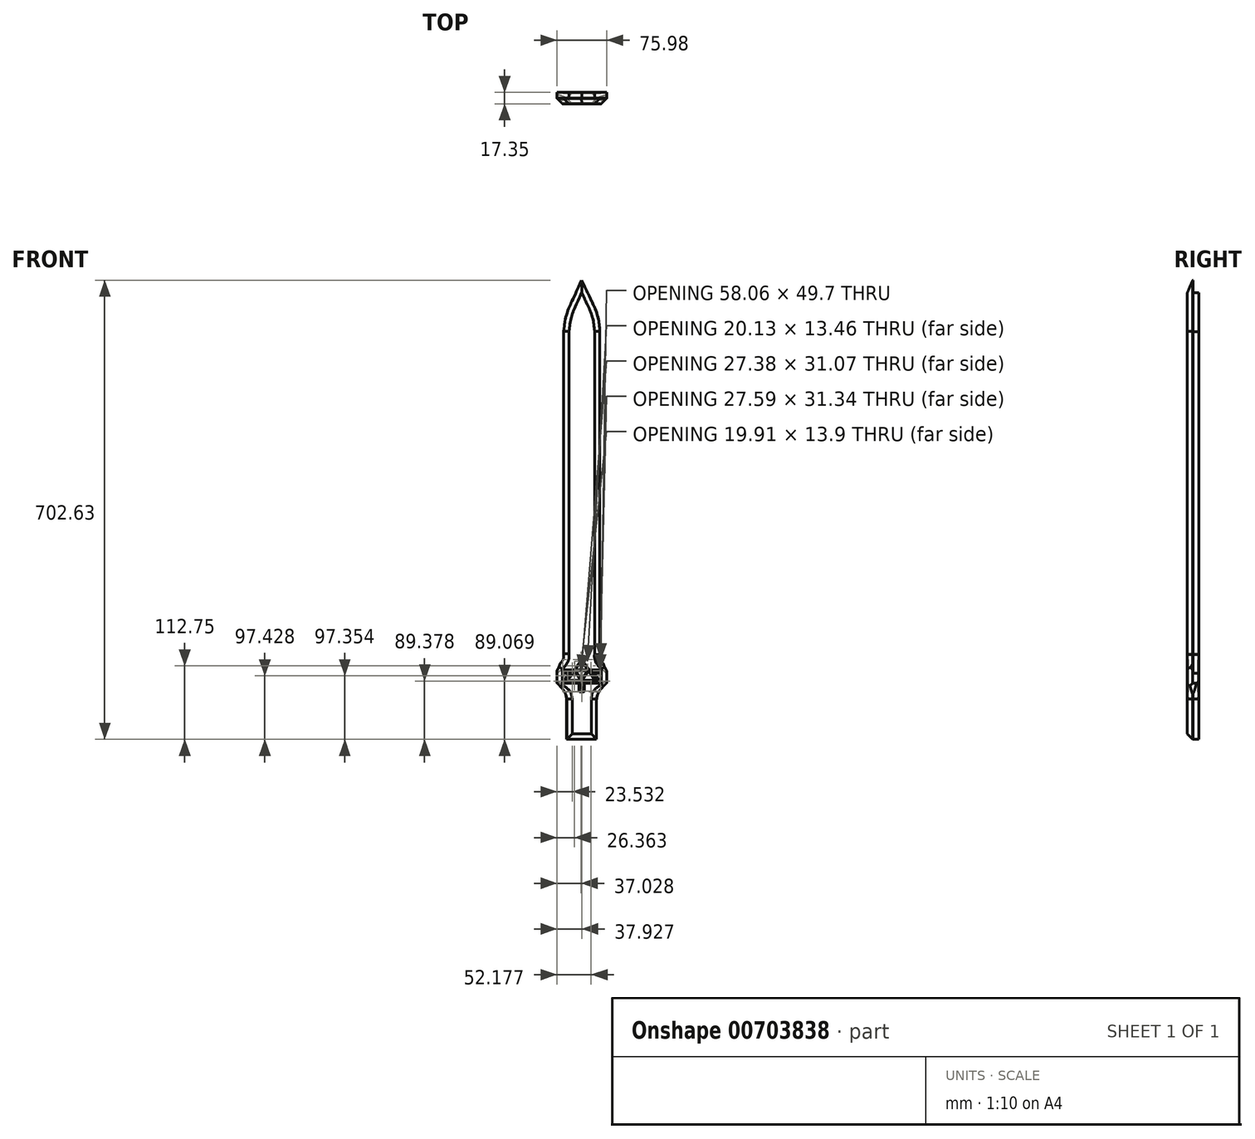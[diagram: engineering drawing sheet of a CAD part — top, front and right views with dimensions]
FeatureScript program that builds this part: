
annotation { "Feature Type Name" : "Feature", "Feature Type Description" : "" }
export const myFeature = defineFeature(function(context is Context, id is Id, definition is map)
    precondition{}
    {
        {
            var Q0;
            Q0=qCreatedBy(makeId("Front.planeOp"),FACE);
            var sketch = newSketch(context, id + "F0", { "sketchPlane" : qUnion([Q0])});
            skLineSegment(sketch, "E0", {"start": v(-23.18, 89.36) * mm, "end": v(-23.18, 27.94) * mm});
            skLineSegment(sketch, "E1", {"start": v(-23.18, 27.94) * mm, "end": v(22.75, 27.94) * mm});
            skLineSegment(sketch, "E2", {"start": v(22.75, 27.94) * mm, "end": v(22.75, 89.36) * mm});
            skFitSpline(sketch, "E3", {"points": [v(-23.18, 89.36) * mm, v(-25.2, 98.78) * mm, v(-29.58, 105.34) * mm, v(-34.12, 110.56) * mm, v(-37.82, 114.26) * mm], "startDerivative": vector(-4.45, 34.79) * mm, "endDerivative": vector(-17.26, 16.67) * mm});
            skFitSpline(sketch, "E4", {"points": [v(22.75, 89.36) * mm, v(24.94, 98.27) * mm, v(29.82, 105.5) * mm, v(34.53, 110.56) * mm, v(38.16, 114.22) * mm], "startDerivative": vector(5.26, 33.12) * mm, "endDerivative": vector(16.94, 16.97) * mm});
            skLineSegment(sketch, "E5", {"start": v(-37.82, 114.26) * mm, "end": v(-37.82, 132.92) * mm});
            skLineSegment(sketch, "E6", {"start": v(38.16, 114.22) * mm, "end": v(38.16, 132.92) * mm});
            skFitSpline(sketch, "E7", {"points": [v(-37.82, 132.92) * mm, v(-34.87, 138.92) * mm, v(-32.96, 144.16) * mm, v(-31.8, 152.09) * mm, v(-31.68, 159) * mm], "startDerivative": vector(12.58, 24.9) * mm, "endDerivative": vector(-0.2, 26.4) * mm});
            skFitSpline(sketch, "E8", {"points": [v(38.16, 132.92) * mm, v(35.43, 137.9) * mm, v(32.87, 144.8) * mm, v(31.98, 152.47) * mm, v(31.85, 157.97) * mm], "startDerivative": vector(-11.86, 20.42) * mm, "endDerivative": vector(-0.27, 22.84) * mm});
            skLineSegment(sketch, "E9", {"start": v(-31.68, 159) * mm, "end": v(-31.68, 655.53) * mm});
            skLineSegment(sketch, "E10", {"start": v(31.85, 157.97) * mm, "end": v(31.87, 655.53) * mm});
            skFitSpline(sketch, "E11", {"points": [v(0, 770.67) * mm, v(5.75, 755.45) * mm, v(13.9, 732.8) * mm, v(20.44, 712.09) * mm, v(27.87, 687.66) * mm, v(30.7, 671.38) * mm, v(31.87, 655.53) * mm], "startDerivative": vector(35.97, -94.67) * mm, "endDerivative": vector(6.36, -107.63) * mm});
            skFitSpline(sketch, "E12", {"points": [v(0, 770.67) * mm, v(-7.17, 751.02) * mm, v(-17.08, 723.77) * mm, v(-25.22, 697.22) * mm, v(-28.94, 682) * mm, v(-31.68, 655.53) * mm], "startDerivative": vector(-36.3, -100.65) * mm, "endDerivative": vector(-10.82, -136.16) * mm});
            skSolve(sketch);
        }
        {
            var Q0;
            Q0=makeQuery(id+"F0.imprint","IMPRINT",FACE,{"disambiguationData":[TD([[makeQuery(id+"F0.imprint","IMPRINT",EDGE,{"derivedFrom":sQuery(id+"F0.wireOp",EDGE,"E0")}),1.0]])]});
            extrude(context, id + "F1", {"entities" : qUnion([Q0]), "depth" : 0.25 * mm, "offsetDistance" : 25.4 * mm});
        }
        {
            var Q0;
            Q0=makeQuery(id+"F1.opExtrude","CAP_FACE",FACE,{"disambiguationData":[OSD([sQuery(id+"F0.wireOp",EDGE,"E0"),sQuery(id+"F0.wireOp",EDGE,"E1"),sQuery(id+"F0.wireOp",EDGE,"E2"),sQuery(id+"F0.wireOp",EDGE,"E3"),sQuery(id+"F0.wireOp",EDGE,"E4"),sQuery(id+"F0.wireOp",EDGE,"E5"),sQuery(id+"F0.wireOp",EDGE,"E6"),sQuery(id+"F0.wireOp",EDGE,"E7"),sQuery(id+"F0.wireOp",EDGE,"E8"),sQuery(id+"F0.wireOp",EDGE,"E9"),sQuery(id+"F0.wireOp",EDGE,"E10"),sQuery(id+"F0.wireOp",EDGE,"E11"),sQuery(id+"F0.wireOp",EDGE,"E12")])],"isStart":true});
            extrude(context, id + "F2", {"entities" : qUnion([Q0]), "operationType" : NewBodyOperationType.ADD, "depth" : 0.25 * mm, "offsetDistance" : 25.4 * mm});
        }
        {
            var Q0;
            Q0=makeQuery(id+"F2.opExtrude","CAP_FACE",FACE,{"disambiguationData":[OSD([sQuery(id+"F0.wireOp",EDGE,"E0"),sQuery(id+"F0.wireOp",EDGE,"E1"),sQuery(id+"F0.wireOp",EDGE,"E2"),sQuery(id+"F0.wireOp",EDGE,"E3"),sQuery(id+"F0.wireOp",EDGE,"E4"),sQuery(id+"F0.wireOp",EDGE,"E5"),sQuery(id+"F0.wireOp",EDGE,"E6"),sQuery(id+"F0.wireOp",EDGE,"E7"),sQuery(id+"F0.wireOp",EDGE,"E8"),sQuery(id+"F0.wireOp",EDGE,"E9"),sQuery(id+"F0.wireOp",EDGE,"E10"),sQuery(id+"F0.wireOp",EDGE,"E11"),sQuery(id+"F0.wireOp",EDGE,"E12")])],"isStart":false});
            var sketch = newSketch(context, id + "F3", { "sketchPlane" : qUnion([Q0])});
            skLineSegment(sketch, "E13", {"start": v(-14.88, 27.94) * mm, "end": v(-14.88, 90.23) * mm});
            skFitSpline(sketch, "E14", {"points": [v(-14.88, 90.23) * mm, v(-16.73, 99.87) * mm, v(-22.43, 106.47) * mm, v(-31.13, 113.07) * mm, v(-38.16, 117.57) * mm], "startDerivative": vector(-3.35, 40.52) * mm, "endDerivative": vector(-28.93, 17.8) * mm});
            skLineSegment(sketch, "E15", {"start": v(14.47, 27.94) * mm, "end": v(14.47, 90.23) * mm});
            skFitSpline(sketch, "E16", {"points": [v(14.47, 90.23) * mm, v(16.95, 99.87) * mm, v(22.69, 106.47) * mm, v(31.86, 113.07) * mm, v(37.82, 117.57) * mm], "startDerivative": vector(6.55, 39.9) * mm, "endDerivative": vector(24.56, 19.23) * mm});
            skFitSpline(sketch, "E17", {"points": [v(37.82, 129.66) * mm, v(28.49, 136.84) * mm, v(22.69, 144.12) * mm, v(19.73, 151.4) * mm, v(19.42, 158.88) * mm], "startDerivative": vector(-34.92, 24.3) * mm, "endDerivative": vector(1.06, 33.21) * mm});
            skFitSpline(sketch, "E18", {"points": [v(-38.16, 129.14) * mm, v(-30.17, 135.78) * mm, v(-23.73, 142.32) * mm, v(-20.88, 147.8) * mm, v(-19.51, 153.3) * mm, v(-19.62, 158.04) * mm], "startDerivative": vector(33.35, 27.05) * mm, "endDerivative": vector(-2.46, 28.44) * mm});
            skLineSegment(sketch, "E19", {"start": v(-19.62, 158.04) * mm, "end": v(-19.62, 652.03) * mm});
            skLineSegment(sketch, "E20", {"start": v(19.42, 158.88) * mm, "end": v(19.33, 652.03) * mm});
            skFitSpline(sketch, "E21", {"points": [v(19.33, 652.03) * mm, v(15.9, 673.87) * mm, v(8.12, 693.88) * mm, v(0, 711.54) * mm], "startDerivative": vector(-6.72, 64.73) * mm, "endDerivative": vector(-25.08, 54.21) * mm});
            skFitSpline(sketch, "E22", {"points": [v(-19.62, 652.03) * mm, v(-16.6, 673.4) * mm, v(-8.12, 694.59) * mm, v(0, 711.54) * mm], "startDerivative": vector(4.95, 63.37) * mm, "endDerivative": vector(25.12, 52.1) * mm});
            skSolve(sketch);
        }
        {
            var Q0;
            {var subQ4=sQuery(id+"F3.wireOp",EDGE,"E13");Q0=makeQuery(id+"F3.imprint","IMPRINT",FACE,{"disambiguationData":[TD([[makeQuery(id+"F3.imprint","IMPRINT",EDGE,{"derivedFrom":subQ4}),-1.0]])]});}
            extrude(context, id + "F4", {"entities" : qUnion([Q0]), "operationType" : NewBodyOperationType.ADD, "depth" : 12.7 * mm, "offsetDistance" : 25.4 * mm});
        }
        {
            var Q0;
            Q0=makeQuery(id+"F4.opExtrude","CAP_FACE",FACE,{"disambiguationData":[OSD([sQuery(id+"F0.wireOp",EDGE,"E1"),sQuery(id+"F0.wireOp",EDGE,"E5"),sQuery(id+"F0.wireOp",EDGE,"E6"),sQuery(id+"F3.wireOp",EDGE,"E13"),sQuery(id+"F3.wireOp",EDGE,"E14"),sQuery(id+"F3.wireOp",EDGE,"E15"),sQuery(id+"F3.wireOp",EDGE,"E16"),sQuery(id+"F3.wireOp",EDGE,"E17"),sQuery(id+"F3.wireOp",EDGE,"E18"),sQuery(id+"F3.wireOp",EDGE,"E19"),sQuery(id+"F3.wireOp",EDGE,"E20"),sQuery(id+"F3.wireOp",EDGE,"E21"),sQuery(id+"F3.wireOp",EDGE,"E22")])],"isStart":false});
            extrude(context, id + "F5", {"entities" : qUnion([Q0]), "operationType" : NewBodyOperationType.ADD, "oppositeDirection" : true, "depth" : 25.9 * mm, "offsetDistance" : 25.4 * mm});
        }
        {
            var Q0;
            Q0=makeQuery(id+"F4.opExtrude","CAP_EDGE",EDGE,{"disambiguationData":[OSD([sQuery(id+"F3.wireOp",EDGE,"E22")])],"isStart":true});
            var Q1;
            Q1=makeQuery(id+"F4.opExtrude","CAP_EDGE",EDGE,{"disambiguationData":[OSD([sQuery(id+"F3.wireOp",EDGE,"E19")])],"isStart":true});
            var Q2;
            Q2=makeQuery(id+"F4.opExtrude","CAP_EDGE",EDGE,{"disambiguationData":[OSD([sQuery(id+"F3.wireOp",EDGE,"E21")])],"isStart":true});
            var Q3;
            Q3=makeQuery(id+"F4.opExtrude","CAP_EDGE",EDGE,{"disambiguationData":[OSD([sQuery(id+"F3.wireOp",EDGE,"E20")])],"isStart":true});
            var Q4;
            Q4=makeQuery(id+"F4.opExtrude","CAP_EDGE",EDGE,{"disambiguationData":[OSD([sQuery(id+"F3.wireOp",EDGE,"E17")])],"isStart":true});
            var Q5;
            Q5=makeQuery(id+"F4.opExtrude","CAP_EDGE",EDGE,{"disambiguationData":[OSD([sQuery(id+"F3.wireOp",EDGE,"E18")])],"isStart":true});
            var Q6;
            Q6=makeQuery(id+"F4.opExtrude","CAP_EDGE",EDGE,{"disambiguationData":[OSD([sQuery(id+"F3.wireOp",EDGE,"E14")])],"isStart":true});
            var Q7;
            Q7=makeQuery(id+"F4.opExtrude","CAP_EDGE",EDGE,{"disambiguationData":[OSD([sQuery(id+"F3.wireOp",EDGE,"E16")])],"isStart":true});
            var Q8;
            Q8=makeQuery(id+"F4.opExtrude","CAP_EDGE",EDGE,{"disambiguationData":[OSD([sQuery(id+"F3.wireOp",EDGE,"E15")])],"isStart":true});
            var Q9;
            Q9=makeQuery(id+"F4.opExtrude","CAP_EDGE",EDGE,{"disambiguationData":[OSD([sQuery(id+"F3.wireOp",EDGE,"E13")])],"isStart":true});
            chamfer(context, id + "F6", {"entities" : qUnion([Q0, Q1, Q2, Q3, Q4, Q5, Q6, Q7, Q8, Q9]), "chamferType" : ChamferType.OFFSET_ANGLE, "width" : 8.13 * mm, "oppositeDirection" : false, "angle" : 47 * degree, "tangentPropagation" : true});
        }
        {
            var Q0;
            Q0=makeQuery(id+"F5.boolean.opBoolean","INTERSECT",EDGE,{"derivedFrom":[makeQuery(id+"F1.opExtrude","CAP_FACE",FACE,{"disambiguationData":[OSD([sQuery(id+"F0.wireOp",EDGE,"E0"),sQuery(id+"F0.wireOp",EDGE,"E1"),sQuery(id+"F0.wireOp",EDGE,"E2"),sQuery(id+"F0.wireOp",EDGE,"E3"),sQuery(id+"F0.wireOp",EDGE,"E4"),sQuery(id+"F0.wireOp",EDGE,"E5"),sQuery(id+"F0.wireOp",EDGE,"E6"),sQuery(id+"F0.wireOp",EDGE,"E7"),sQuery(id+"F0.wireOp",EDGE,"E8"),sQuery(id+"F0.wireOp",EDGE,"E9"),sQuery(id+"F0.wireOp",EDGE,"E10"),sQuery(id+"F0.wireOp",EDGE,"E11"),sQuery(id+"F0.wireOp",EDGE,"E12")])],"isStart":false}),makeQuery(id+"F5.opExtrude","SWEPT_FACE",FACE,{"disambiguationData":[OSD([sQuery(id+"F3.wireOp",EDGE,"E20")])]})]});
            var Q1;
            Q1=makeQuery(id+"F5.boolean.opBoolean","INTERSECT",EDGE,{"derivedFrom":[makeQuery(id+"F1.opExtrude","CAP_FACE",FACE,{"disambiguationData":[OSD([sQuery(id+"F0.wireOp",EDGE,"E0"),sQuery(id+"F0.wireOp",EDGE,"E1"),sQuery(id+"F0.wireOp",EDGE,"E2"),sQuery(id+"F0.wireOp",EDGE,"E3"),sQuery(id+"F0.wireOp",EDGE,"E4"),sQuery(id+"F0.wireOp",EDGE,"E5"),sQuery(id+"F0.wireOp",EDGE,"E6"),sQuery(id+"F0.wireOp",EDGE,"E7"),sQuery(id+"F0.wireOp",EDGE,"E8"),sQuery(id+"F0.wireOp",EDGE,"E9"),sQuery(id+"F0.wireOp",EDGE,"E10"),sQuery(id+"F0.wireOp",EDGE,"E11"),sQuery(id+"F0.wireOp",EDGE,"E12")])],"isStart":false}),makeQuery(id+"F5.opExtrude","SWEPT_FACE",FACE,{"disambiguationData":[OSD([sQuery(id+"F3.wireOp",EDGE,"E17")])]})]});
            var Q2;
            Q2=makeQuery(id+"F5.boolean.opBoolean","INTERSECT",EDGE,{"derivedFrom":[makeQuery(id+"F1.opExtrude","CAP_FACE",FACE,{"disambiguationData":[OSD([sQuery(id+"F0.wireOp",EDGE,"E0"),sQuery(id+"F0.wireOp",EDGE,"E1"),sQuery(id+"F0.wireOp",EDGE,"E2"),sQuery(id+"F0.wireOp",EDGE,"E3"),sQuery(id+"F0.wireOp",EDGE,"E4"),sQuery(id+"F0.wireOp",EDGE,"E5"),sQuery(id+"F0.wireOp",EDGE,"E6"),sQuery(id+"F0.wireOp",EDGE,"E7"),sQuery(id+"F0.wireOp",EDGE,"E8"),sQuery(id+"F0.wireOp",EDGE,"E9"),sQuery(id+"F0.wireOp",EDGE,"E10"),sQuery(id+"F0.wireOp",EDGE,"E11"),sQuery(id+"F0.wireOp",EDGE,"E12")])],"isStart":false}),makeQuery(id+"F5.opExtrude","SWEPT_FACE",FACE,{"disambiguationData":[OSD([sQuery(id+"F3.wireOp",EDGE,"E16")])]})]});
            var Q3;
            Q3=makeQuery(id+"F5.boolean.opBoolean","INTERSECT",EDGE,{"derivedFrom":[makeQuery(id+"F1.opExtrude","CAP_FACE",FACE,{"disambiguationData":[OSD([sQuery(id+"F0.wireOp",EDGE,"E0"),sQuery(id+"F0.wireOp",EDGE,"E1"),sQuery(id+"F0.wireOp",EDGE,"E2"),sQuery(id+"F0.wireOp",EDGE,"E3"),sQuery(id+"F0.wireOp",EDGE,"E4"),sQuery(id+"F0.wireOp",EDGE,"E5"),sQuery(id+"F0.wireOp",EDGE,"E6"),sQuery(id+"F0.wireOp",EDGE,"E7"),sQuery(id+"F0.wireOp",EDGE,"E8"),sQuery(id+"F0.wireOp",EDGE,"E9"),sQuery(id+"F0.wireOp",EDGE,"E10"),sQuery(id+"F0.wireOp",EDGE,"E11"),sQuery(id+"F0.wireOp",EDGE,"E12")])],"isStart":false}),makeQuery(id+"F5.opExtrude","SWEPT_FACE",FACE,{"disambiguationData":[OSD([sQuery(id+"F3.wireOp",EDGE,"E15")])]})]});
            var Q4;
            Q4=makeQuery(id+"F5.boolean.opBoolean","INTERSECT",EDGE,{"derivedFrom":[makeQuery(id+"F1.opExtrude","CAP_FACE",FACE,{"disambiguationData":[OSD([sQuery(id+"F0.wireOp",EDGE,"E0"),sQuery(id+"F0.wireOp",EDGE,"E1"),sQuery(id+"F0.wireOp",EDGE,"E2"),sQuery(id+"F0.wireOp",EDGE,"E3"),sQuery(id+"F0.wireOp",EDGE,"E4"),sQuery(id+"F0.wireOp",EDGE,"E5"),sQuery(id+"F0.wireOp",EDGE,"E6"),sQuery(id+"F0.wireOp",EDGE,"E7"),sQuery(id+"F0.wireOp",EDGE,"E8"),sQuery(id+"F0.wireOp",EDGE,"E9"),sQuery(id+"F0.wireOp",EDGE,"E10"),sQuery(id+"F0.wireOp",EDGE,"E11"),sQuery(id+"F0.wireOp",EDGE,"E12")])],"isStart":false}),makeQuery(id+"F5.opExtrude","SWEPT_FACE",FACE,{"disambiguationData":[OSD([sQuery(id+"F3.wireOp",EDGE,"E13")])]})]});
            var Q5;
            Q5=makeQuery(id+"F5.boolean.opBoolean","INTERSECT",EDGE,{"derivedFrom":[makeQuery(id+"F1.opExtrude","CAP_FACE",FACE,{"disambiguationData":[OSD([sQuery(id+"F0.wireOp",EDGE,"E0"),sQuery(id+"F0.wireOp",EDGE,"E1"),sQuery(id+"F0.wireOp",EDGE,"E2"),sQuery(id+"F0.wireOp",EDGE,"E3"),sQuery(id+"F0.wireOp",EDGE,"E4"),sQuery(id+"F0.wireOp",EDGE,"E5"),sQuery(id+"F0.wireOp",EDGE,"E6"),sQuery(id+"F0.wireOp",EDGE,"E7"),sQuery(id+"F0.wireOp",EDGE,"E8"),sQuery(id+"F0.wireOp",EDGE,"E9"),sQuery(id+"F0.wireOp",EDGE,"E10"),sQuery(id+"F0.wireOp",EDGE,"E11"),sQuery(id+"F0.wireOp",EDGE,"E12")])],"isStart":false}),makeQuery(id+"F5.opExtrude","SWEPT_FACE",FACE,{"disambiguationData":[OSD([sQuery(id+"F3.wireOp",EDGE,"E14")])]})]});
            var Q6;
            Q6=makeQuery(id+"F5.boolean.opBoolean","INTERSECT",EDGE,{"derivedFrom":[makeQuery(id+"F1.opExtrude","CAP_FACE",FACE,{"disambiguationData":[OSD([sQuery(id+"F0.wireOp",EDGE,"E0"),sQuery(id+"F0.wireOp",EDGE,"E1"),sQuery(id+"F0.wireOp",EDGE,"E2"),sQuery(id+"F0.wireOp",EDGE,"E3"),sQuery(id+"F0.wireOp",EDGE,"E4"),sQuery(id+"F0.wireOp",EDGE,"E5"),sQuery(id+"F0.wireOp",EDGE,"E6"),sQuery(id+"F0.wireOp",EDGE,"E7"),sQuery(id+"F0.wireOp",EDGE,"E8"),sQuery(id+"F0.wireOp",EDGE,"E9"),sQuery(id+"F0.wireOp",EDGE,"E10"),sQuery(id+"F0.wireOp",EDGE,"E11"),sQuery(id+"F0.wireOp",EDGE,"E12")])],"isStart":false}),makeQuery(id+"F5.opExtrude","SWEPT_FACE",FACE,{"disambiguationData":[OSD([sQuery(id+"F3.wireOp",EDGE,"E18")])]})]});
            var Q7;
            Q7=makeQuery(id+"F5.boolean.opBoolean","INTERSECT",EDGE,{"derivedFrom":[makeQuery(id+"F1.opExtrude","CAP_FACE",FACE,{"disambiguationData":[OSD([sQuery(id+"F0.wireOp",EDGE,"E0"),sQuery(id+"F0.wireOp",EDGE,"E1"),sQuery(id+"F0.wireOp",EDGE,"E2"),sQuery(id+"F0.wireOp",EDGE,"E3"),sQuery(id+"F0.wireOp",EDGE,"E4"),sQuery(id+"F0.wireOp",EDGE,"E5"),sQuery(id+"F0.wireOp",EDGE,"E6"),sQuery(id+"F0.wireOp",EDGE,"E7"),sQuery(id+"F0.wireOp",EDGE,"E8"),sQuery(id+"F0.wireOp",EDGE,"E9"),sQuery(id+"F0.wireOp",EDGE,"E10"),sQuery(id+"F0.wireOp",EDGE,"E11"),sQuery(id+"F0.wireOp",EDGE,"E12")])],"isStart":false}),makeQuery(id+"F5.opExtrude","SWEPT_FACE",FACE,{"disambiguationData":[OSD([sQuery(id+"F3.wireOp",EDGE,"E19")])]})]});
            var Q8;
            Q8=makeQuery(id+"F5.boolean.opBoolean","INTERSECT",EDGE,{"derivedFrom":[makeQuery(id+"F1.opExtrude","CAP_FACE",FACE,{"disambiguationData":[OSD([sQuery(id+"F0.wireOp",EDGE,"E0"),sQuery(id+"F0.wireOp",EDGE,"E1"),sQuery(id+"F0.wireOp",EDGE,"E2"),sQuery(id+"F0.wireOp",EDGE,"E3"),sQuery(id+"F0.wireOp",EDGE,"E4"),sQuery(id+"F0.wireOp",EDGE,"E5"),sQuery(id+"F0.wireOp",EDGE,"E6"),sQuery(id+"F0.wireOp",EDGE,"E7"),sQuery(id+"F0.wireOp",EDGE,"E8"),sQuery(id+"F0.wireOp",EDGE,"E9"),sQuery(id+"F0.wireOp",EDGE,"E10"),sQuery(id+"F0.wireOp",EDGE,"E11"),sQuery(id+"F0.wireOp",EDGE,"E12")])],"isStart":false}),makeQuery(id+"F5.opExtrude","SWEPT_FACE",FACE,{"disambiguationData":[OSD([sQuery(id+"F3.wireOp",EDGE,"E22")])]})]});
            var Q9;
            Q9=makeQuery(id+"F5.boolean.opBoolean","INTERSECT",EDGE,{"derivedFrom":[makeQuery(id+"F1.opExtrude","CAP_FACE",FACE,{"disambiguationData":[OSD([sQuery(id+"F0.wireOp",EDGE,"E0"),sQuery(id+"F0.wireOp",EDGE,"E1"),sQuery(id+"F0.wireOp",EDGE,"E2"),sQuery(id+"F0.wireOp",EDGE,"E3"),sQuery(id+"F0.wireOp",EDGE,"E4"),sQuery(id+"F0.wireOp",EDGE,"E5"),sQuery(id+"F0.wireOp",EDGE,"E6"),sQuery(id+"F0.wireOp",EDGE,"E7"),sQuery(id+"F0.wireOp",EDGE,"E8"),sQuery(id+"F0.wireOp",EDGE,"E9"),sQuery(id+"F0.wireOp",EDGE,"E10"),sQuery(id+"F0.wireOp",EDGE,"E11"),sQuery(id+"F0.wireOp",EDGE,"E12")])],"isStart":false}),makeQuery(id+"F5.opExtrude","SWEPT_FACE",FACE,{"disambiguationData":[OSD([sQuery(id+"F3.wireOp",EDGE,"E21")])]})]});
            chamfer(context, id + "F7", {"entities" : qUnion([Q0, Q1, Q2, Q3, Q4, Q5, Q6, Q7, Q8, Q9]), "width" : 8.13 * mm, "tangentPropagation" : true});
        }
        {
            var Q0;
            Q0=makeQuery(id+"F5.opExtrude","CAP_FACE",FACE,{"disambiguationData":[OSD([sQuery(id+"F0.wireOp",EDGE,"E1"),sQuery(id+"F0.wireOp",EDGE,"E5"),sQuery(id+"F0.wireOp",EDGE,"E6"),sQuery(id+"F3.wireOp",EDGE,"E13"),sQuery(id+"F3.wireOp",EDGE,"E14"),sQuery(id+"F3.wireOp",EDGE,"E15"),sQuery(id+"F3.wireOp",EDGE,"E16"),sQuery(id+"F3.wireOp",EDGE,"E17"),sQuery(id+"F3.wireOp",EDGE,"E18"),sQuery(id+"F3.wireOp",EDGE,"E19"),sQuery(id+"F3.wireOp",EDGE,"E20"),sQuery(id+"F3.wireOp",EDGE,"E21"),sQuery(id+"F3.wireOp",EDGE,"E22")])],"isStart":false});
            extrude(context, id + "F8", {"entities" : qUnion([Q0]), "operationType" : NewBodyOperationType.REMOVE, "oppositeDirection" : true, "depth" : 5.33 * mm, "offsetDistance" : 25.4 * mm});
        }
        {
            var Q0;
            Q0=makeQuery(id+"F4.opExtrude","CAP_FACE",FACE,{"disambiguationData":[OSD([sQuery(id+"F0.wireOp",EDGE,"E1"),sQuery(id+"F0.wireOp",EDGE,"E5"),sQuery(id+"F0.wireOp",EDGE,"E6"),sQuery(id+"F3.wireOp",EDGE,"E13"),sQuery(id+"F3.wireOp",EDGE,"E14"),sQuery(id+"F3.wireOp",EDGE,"E15"),sQuery(id+"F3.wireOp",EDGE,"E16"),sQuery(id+"F3.wireOp",EDGE,"E17"),sQuery(id+"F3.wireOp",EDGE,"E18"),sQuery(id+"F3.wireOp",EDGE,"E19"),sQuery(id+"F3.wireOp",EDGE,"E20"),sQuery(id+"F3.wireOp",EDGE,"E21"),sQuery(id+"F3.wireOp",EDGE,"E22")])],"isStart":false});
            extrude(context, id + "F9", {"entities" : qUnion([Q0]), "operationType" : NewBodyOperationType.REMOVE, "oppositeDirection" : true, "depth" : 4 * mm, "offsetDistance" : 25.4 * mm});
        }
        {
            var Q0;
            {var subQ0=sQuery(id+"F0.wireOp",EDGE,"E12");var subQ1=sQuery(id+"F0.wireOp",EDGE,"E11");var subQ2=sQuery(id+"F0.wireOp",EDGE,"E10");var subQ3=sQuery(id+"F0.wireOp",EDGE,"E9");var subQ4=sQuery(id+"F0.wireOp",EDGE,"E8");var subQ5=sQuery(id+"F0.wireOp",EDGE,"E7");var subQ6=sQuery(id+"F0.wireOp",EDGE,"E6");var subQ7=sQuery(id+"F0.wireOp",EDGE,"E5");Q0=makeQuery(id+"F5.boolean.opBoolean","SPLIT",FACE,{"disambiguationData":[TD([makeQuery(id+"F1.opExtrude","SWEPT_FACE",FACE,{"disambiguationData":[OSD([subQ5])]})])],"derivedFrom":makeQuery(id+"F1.opExtrude","CAP_FACE",FACE,{"disambiguationData":[OSD([sQuery(id+"F0.wireOp",EDGE,"E0"),sQuery(id+"F0.wireOp",EDGE,"E1"),sQuery(id+"F0.wireOp",EDGE,"E2"),sQuery(id+"F0.wireOp",EDGE,"E3"),sQuery(id+"F0.wireOp",EDGE,"E4"),subQ7,subQ6,subQ5,subQ4,subQ3,subQ2,subQ1,subQ0])],"isStart":false})});}
            extrude(context, id + "F10", {"entities" : qUnion([Q0]), "operationType" : NewBodyOperationType.REMOVE, "oppositeDirection" : true, "depth" : 25.4 * mm, "offsetDistance" : 25.4 * mm});
        }
        {
            var Q0;
            Q0=makeQuery(id+"F8.boolean.opBoolean","COPY",FACE,{"derivedFrom":makeQuery(id+"F8.opExtrude","CAP_FACE",FACE,{"disambiguationData":[OSD([sQuery(id+"F0.wireOp",EDGE,"E1"),sQuery(id+"F0.wireOp",EDGE,"E5"),sQuery(id+"F0.wireOp",EDGE,"E6"),sQuery(id+"F3.wireOp",EDGE,"E13"),sQuery(id+"F3.wireOp",EDGE,"E14"),sQuery(id+"F3.wireOp",EDGE,"E15"),sQuery(id+"F3.wireOp",EDGE,"E16"),sQuery(id+"F3.wireOp",EDGE,"E17"),sQuery(id+"F3.wireOp",EDGE,"E18"),sQuery(id+"F3.wireOp",EDGE,"E19"),sQuery(id+"F3.wireOp",EDGE,"E20"),sQuery(id+"F3.wireOp",EDGE,"E21"),sQuery(id+"F3.wireOp",EDGE,"E22")])],"isStart":false})});
            extrude(context, id + "F11", {"entities" : qUnion([Q0]), "operationType" : NewBodyOperationType.ADD, "depth" : 0.76 * mm, "offsetDistance" : 25.4 * mm});
        }
        {
            var Q0;
            Q0=makeQuery(id+"F9.boolean.opBoolean","COPY",FACE,{"derivedFrom":makeQuery(id+"F9.opExtrude","CAP_FACE",FACE,{"disambiguationData":[OSD([sQuery(id+"F0.wireOp",EDGE,"E1"),sQuery(id+"F0.wireOp",EDGE,"E5"),sQuery(id+"F0.wireOp",EDGE,"E6"),sQuery(id+"F3.wireOp",EDGE,"E13"),sQuery(id+"F3.wireOp",EDGE,"E14"),sQuery(id+"F3.wireOp",EDGE,"E15"),sQuery(id+"F3.wireOp",EDGE,"E16"),sQuery(id+"F3.wireOp",EDGE,"E17"),sQuery(id+"F3.wireOp",EDGE,"E18"),sQuery(id+"F3.wireOp",EDGE,"E19"),sQuery(id+"F3.wireOp",EDGE,"E20"),sQuery(id+"F3.wireOp",EDGE,"E21"),sQuery(id+"F3.wireOp",EDGE,"E22")])],"isStart":false})});
            var sketch = newSketch(context, id + "F12", { "sketchPlane" : qUnion([Q0])});
            skLineSegment(sketch, "E23", {"start": v(-11.79, 134.23) * mm, "end": v(0, 150.22) * mm});
            skLineSegment(sketch, "E24", {"start": v(0, 150.22) * mm, "end": v(12.06, 133.96) * mm});
            skLineSegment(sketch, "E25", {"start": v(12.06, 133.96) * mm, "end": v(26.89, 133.96) * mm});
            skLineSegment(sketch, "E26", {"start": v(26.89, 129.23) * mm, "end": v(19.36, 129.23) * mm});
            skLineSegment(sketch, "E27", {"start": v(19.36, 129.23) * mm, "end": v(27.93, 116.9) * mm});
            skLineSegment(sketch, "E28", {"start": v(26.89, 114) * mm, "end": v(4.81, 114) * mm});
            skLineSegment(sketch, "E29", {"start": v(-5.35, 114) * mm, "end": v(-27.24, 114) * mm});
            skLineSegment(sketch, "E30", {"start": v(-27.9, 116.9) * mm, "end": v(-19.08, 129.43) * mm});
            skLineSegment(sketch, "E31", {"start": v(-19.08, 129.43) * mm, "end": v(-27.24, 129.43) * mm});
            skLineSegment(sketch, "E32", {"start": v(-11.79, 134.23) * mm, "end": v(-27.24, 134.23) * mm});
            skLineSegment(sketch, "E33", {"start": v(0, 147.42) * mm, "end": v(-9.27, 134.23) * mm});
            skLineSegment(sketch, "E34", {"start": v(-9.27, 134.23) * mm, "end": v(10.86, 133.96) * mm});
            skLineSegment(sketch, "E35", {"start": v(10.86, 133.96) * mm, "end": v(0, 147.42) * mm});
            skLineSegment(sketch, "E36", {"start": v(-11.79, 132.99) * mm, "end": v(-21.8, 119.4) * mm});
            skLineSegment(sketch, "E37", {"start": v(-21.25, 117.57) * mm, "end": v(-0.56, 117.57) * mm});
            skLineSegment(sketch, "E38", {"start": v(-0.56, 117.57) * mm, "end": v(-0.56, 102.3) * mm});
            skLineSegment(sketch, "E39", {"start": v(-4.22, 102.3) * mm, "end": v(-4.22, 113.14) * mm});
            skLineSegment(sketch, "E40", {"start": v(4.21, 113.14) * mm, "end": v(4.21, 102.3) * mm});
            skLineSegment(sketch, "E41", {"start": v(0.6, 102.3) * mm, "end": v(0.6, 117.57) * mm});
            skLineSegment(sketch, "E42", {"start": v(0.6, 117.57) * mm, "end": v(21.41, 117.57) * mm});
            skLineSegment(sketch, "E43", {"start": v(22.25, 118.83) * mm, "end": v(12.3, 132.54) * mm});
            skLineSegment(sketch, "E44", {"start": v(12.3, 132.54) * mm, "end": v(26.89, 132.54) * mm});
            skLineSegment(sketch, "E45", {"start": v(26.89, 130.12) * mm, "end": v(18.73, 130.12) * mm});
            skLineSegment(sketch, "E46", {"start": v(18.4, 128.97) * mm, "end": v(27.24, 116.24) * mm});
            skLineSegment(sketch, "E47", {"start": v(-20.22, 118.34) * mm, "end": v(-10.53, 132.13) * mm});
            skLineSegment(sketch, "E48", {"start": v(-10.53, 132.13) * mm, "end": v(-0.88, 118.24) * mm});
            skLineSegment(sketch, "E49", {"start": v(-0.88, 118.24) * mm, "end": v(-20.22, 118.34) * mm});
            skLineSegment(sketch, "E50", {"start": v(1.5, 118.34) * mm, "end": v(11.28, 132.25) * mm});
            skLineSegment(sketch, "E51", {"start": v(11.28, 132.25) * mm, "end": v(21.41, 118.34) * mm});
            skLineSegment(sketch, "E52", {"start": v(21.41, 118.34) * mm, "end": v(1.5, 118.34) * mm});
            skLineSegment(sketch, "E53", {"start": v(9.51, 132.94) * mm, "end": v(-9.05, 132.94) * mm});
            skLineSegment(sketch, "E54", {"start": v(-9.05, 132.94) * mm, "end": v(0, 119.04) * mm});
            skLineSegment(sketch, "E55", {"start": v(0, 119.04) * mm, "end": v(9.51, 132.94) * mm});
            skFitSpline(sketch, "E56", {"points": [v(-21.25, 117.57) * mm, v(-22.4, 117.93) * mm, v(-21.8, 119.4) * mm], "startDerivative": vector(-3.32, 0.3) * mm, "endDerivative": vector(2.1, 3.3) * mm});
            skFitSpline(sketch, "E57", {"points": [v(-27.24, 114) * mm, v(-28.28, 115.14) * mm, v(-27.9, 116.9) * mm], "startDerivative": vector(-2.88, 2.13) * mm, "endDerivative": vector(1.5, 3.64) * mm});
            skFitSpline(sketch, "E58", {"points": [v(-27.24, 129.43) * mm, v(-28.9, 130.86) * mm, v(-28.84, 133.23) * mm, v(-27.24, 134.23) * mm], "startDerivative": vector(-5.9, 3.35) * mm, "endDerivative": vector(6.04, 2.14) * mm});
            skFitSpline(sketch, "E59", {"points": [v(22.25, 118.83) * mm, v(22.47, 117.72) * mm, v(21.41, 117.57) * mm], "startDerivative": vector(1.1, -2.67) * mm, "endDerivative": vector(-2.78, 0.17) * mm});
            skLineSegment(sketch, "E60", {"start": v(-11.79, 132.99) * mm, "end": v(-27.37, 132.99) * mm});
            skLineSegment(sketch, "E61", {"start": v(26.7, 114.7) * mm, "end": v(4.81, 114.7) * mm});
            skLineSegment(sketch, "E62", {"start": v(3.19, 113.27) * mm, "end": v(3.38, 102.25) * mm});
            skLineSegment(sketch, "E63", {"start": v(-3, 102.25) * mm, "end": v(-3, 113.23) * mm});
            skLineSegment(sketch, "E64", {"start": v(-5.42, 115.26) * mm, "end": v(-26.92, 115.26) * mm});
            skLineSegment(sketch, "E65", {"start": v(-27.2, 116.42) * mm, "end": v(-18, 129.5) * mm});
            skLineSegment(sketch, "E66", {"start": v(-19.1, 130.43) * mm, "end": v(-27.37, 130.43) * mm});
            skFitSpline(sketch, "E67", {"points": [v(-27.37, 132.99) * mm, v(-28.15, 131.74) * mm, v(-27.37, 130.43) * mm], "startDerivative": vector(-2.36, -2.5) * mm, "endDerivative": vector(2.34, -2.6) * mm});
            skFitSpline(sketch, "E68", {"points": [v(26.89, 133.96) * mm, v(28.5, 132.99) * mm, v(28.73, 130.43) * mm, v(26.89, 129.23) * mm], "startDerivative": vector(5.97, -1.95) * mm, "endDerivative": vector(-6.8, -2.42) * mm});
            skFitSpline(sketch, "E69", {"points": [v(26.89, 130.12) * mm, v(27.98, 131.53) * mm, v(26.89, 132.54) * mm], "startDerivative": vector(3.22, 2.86) * mm, "endDerivative": vector(-3.32, 1.98) * mm});
            skFitSpline(sketch, "E70", {"points": [v(18.73, 130.12) * mm, v(18.23, 129.75) * mm, v(18.4, 128.97) * mm], "startDerivative": vector(-1.4, -0.61) * mm, "endDerivative": vector(0.7, -1.65) * mm});
            skFitSpline(sketch, "E71", {"points": [v(27.24, 116.24) * mm, v(27.43, 115.26) * mm, v(26.7, 114.7) * mm], "startDerivative": vector(0.84, -2.13) * mm, "endDerivative": vector(-1.93, -0.96) * mm});
            skFitSpline(sketch, "E72", {"points": [v(27.93, 116.9) * mm, v(28.3, 115.33) * mm, v(27.7, 114.19) * mm, v(26.89, 114) * mm], "startDerivative": vector(1.64, -4.12) * mm, "endDerivative": vector(-3.1, -0.07) * mm});
            skFitSpline(sketch, "E73", {"points": [v(4.81, 114.7) * mm, v(3.92, 114.6) * mm, v(3.37, 114.15) * mm, v(3.19, 113.27) * mm], "startDerivative": vector(-2.72, 0.02) * mm, "endDerivative": vector(-0.22, -2.76) * mm});
            skFitSpline(sketch, "E74", {"points": [v(4.81, 114) * mm, v(4.22, 113.8) * mm, v(4.21, 113.14) * mm], "startDerivative": vector(-1.5, -0.2) * mm, "endDerivative": vector(0.3, -1.52) * mm});
            skFitSpline(sketch, "E75", {"points": [v(4.21, 102.3) * mm, v(3.38, 100.95) * mm, v(1.67, 100.75) * mm, v(0, 101.38) * mm], "startDerivative": vector(-1.94, -4.96) * mm, "endDerivative": vector(-4.65, 2.26) * mm});
            skFitSpline(sketch, "E76", {"points": [v(0.6, 102.3) * mm, v(1.44, 101.61) * mm, v(2.73, 101.58) * mm, v(3.38, 102.25) * mm], "startDerivative": vector(2.16, -2.4) * mm, "endDerivative": vector(1.66, 2.62) * mm});
            skFitSpline(sketch, "E77", {"points": [v(-0.56, 102.3) * mm, v(-1.1, 101.78) * mm, v(-2.42, 101.75) * mm, v(-3, 102.25) * mm], "startDerivative": vector(-1.33, -2) * mm, "endDerivative": vector(-1.49, 1.96) * mm});
            skFitSpline(sketch, "E78", {"points": [v(0, 101.38) * mm, v(-0.56, 100.71) * mm, v(-3, 100.75) * mm, v(-4.22, 102.3) * mm], "startDerivative": vector(-1.43, -3.14) * mm, "endDerivative": vector(-2.38, 5.15) * mm});
            skFitSpline(sketch, "E79", {"points": [v(-3, 113.23) * mm, v(-3, 114.27) * mm, v(-4.01, 115.29) * mm, v(-5.42, 115.26) * mm], "startDerivative": vector(0.63, 3.44) * mm, "endDerivative": vector(-4.15, -0.82) * mm});
            skFitSpline(sketch, "E80", {"points": [v(-5.35, 114) * mm, v(-4.5, 114) * mm, v(-4.22, 113.14) * mm], "startDerivative": vector(2, 0.42) * mm, "endDerivative": vector(0.26, -2.12) * mm});
            skFitSpline(sketch, "E81", {"points": [v(-26.92, 115.26) * mm, v(-27.37, 115.58) * mm, v(-27.2, 116.42) * mm], "startDerivative": vector(-1.3, 0.54) * mm, "endDerivative": vector(0.67, 1.74) * mm});
            skFitSpline(sketch, "E82", {"points": [v(-19.1, 130.43) * mm, v(-18.31, 130.12) * mm, v(-18, 129.5) * mm], "startDerivative": vector(1.7, -0.42) * mm, "endDerivative": vector(0.44, -1.46) * mm});
            skSolve(sketch);
        }
        {
            var Q0;
            Q0=makeQuery(id+"F12.imprint","IMPRINT",FACE,{"disambiguationData":[TD([[makeQuery(id+"F12.imprint","IMPRINT",EDGE,{"derivedFrom":sQuery(id+"F12.wireOp",EDGE,"E23")}),-1.0]])]});
            extrude(context, id + "F13", {"entities" : qUnion([Q0]), "operationType" : NewBodyOperationType.ADD, "depth" : 12.7 * mm, "offsetDistance" : 25.4 * mm});
        }
        {
            var Q0;
            Q0=makeQuery(id+"F13.opExtrude","CAP_FACE",FACE,{"disambiguationData":[OSD([sQuery(id+"F12.wireOp",EDGE,"E23"),sQuery(id+"F12.wireOp",EDGE,"E24"),sQuery(id+"F12.wireOp",EDGE,"E25"),sQuery(id+"F12.wireOp",EDGE,"E26"),sQuery(id+"F12.wireOp",EDGE,"E27"),sQuery(id+"F12.wireOp",EDGE,"E28"),sQuery(id+"F12.wireOp",EDGE,"E29"),sQuery(id+"F12.wireOp",EDGE,"E30"),sQuery(id+"F12.wireOp",EDGE,"E31"),sQuery(id+"F12.wireOp",EDGE,"E32"),sQuery(id+"F12.wireOp",EDGE,"E33"),sQuery(id+"F12.wireOp",EDGE,"E34"),sQuery(id+"F12.wireOp",EDGE,"E35"),sQuery(id+"F12.wireOp",EDGE,"E36"),sQuery(id+"F12.wireOp",EDGE,"E37"),sQuery(id+"F12.wireOp",EDGE,"E38"),sQuery(id+"F12.wireOp",EDGE,"E39"),sQuery(id+"F12.wireOp",EDGE,"E40"),sQuery(id+"F12.wireOp",EDGE,"E41"),sQuery(id+"F12.wireOp",EDGE,"E42"),sQuery(id+"F12.wireOp",EDGE,"E43"),sQuery(id+"F12.wireOp",EDGE,"E44"),sQuery(id+"F12.wireOp",EDGE,"E45"),sQuery(id+"F12.wireOp",EDGE,"E46"),sQuery(id+"F12.wireOp",EDGE,"E47"),sQuery(id+"F12.wireOp",EDGE,"E48"),sQuery(id+"F12.wireOp",EDGE,"E49"),sQuery(id+"F12.wireOp",EDGE,"E50"),sQuery(id+"F12.wireOp",EDGE,"E51"),sQuery(id+"F12.wireOp",EDGE,"E52"),sQuery(id+"F12.wireOp",EDGE,"E53"),sQuery(id+"F12.wireOp",EDGE,"E54"),sQuery(id+"F12.wireOp",EDGE,"E55"),sQuery(id+"F12.wireOp",EDGE,"E56"),sQuery(id+"F12.wireOp",EDGE,"E57"),sQuery(id+"F12.wireOp",EDGE,"E58"),sQuery(id+"F12.wireOp",EDGE,"E59"),sQuery(id+"F12.wireOp",EDGE,"E60"),sQuery(id+"F12.wireOp",EDGE,"E61"),sQuery(id+"F12.wireOp",EDGE,"E62"),sQuery(id+"F12.wireOp",EDGE,"E63"),sQuery(id+"F12.wireOp",EDGE,"E64"),sQuery(id+"F12.wireOp",EDGE,"E65"),sQuery(id+"F12.wireOp",EDGE,"E66"),sQuery(id+"F12.wireOp",EDGE,"E67"),sQuery(id+"F12.wireOp",EDGE,"E68"),sQuery(id+"F12.wireOp",EDGE,"E69"),sQuery(id+"F12.wireOp",EDGE,"E70"),sQuery(id+"F12.wireOp",EDGE,"E71"),sQuery(id+"F12.wireOp",EDGE,"E72"),sQuery(id+"F12.wireOp",EDGE,"E73"),sQuery(id+"F12.wireOp",EDGE,"E74"),sQuery(id+"F12.wireOp",EDGE,"E75"),sQuery(id+"F12.wireOp",EDGE,"E76"),sQuery(id+"F12.wireOp",EDGE,"E77"),sQuery(id+"F12.wireOp",EDGE,"E78"),sQuery(id+"F12.wireOp",EDGE,"E79"),sQuery(id+"F12.wireOp",EDGE,"E80"),sQuery(id+"F12.wireOp",EDGE,"E81"),sQuery(id+"F12.wireOp",EDGE,"E82")])],"isStart":false});
            extrude(context, id + "F14", {"entities" : qUnion([Q0]), "operationType" : NewBodyOperationType.REMOVE, "oppositeDirection" : true, "depth" : 10.16 * mm, "offsetDistance" : 25.4 * mm});
        }
        {
            var Q0;
            Q0=makeQuery(id+"F14.boolean.opBoolean","COPY",FACE,{"derivedFrom":makeQuery(id+"F14.opExtrude","CAP_FACE",FACE,{"disambiguationData":[OSD([sQuery(id+"F12.wireOp",EDGE,"E23"),sQuery(id+"F12.wireOp",EDGE,"E24"),sQuery(id+"F12.wireOp",EDGE,"E25"),sQuery(id+"F12.wireOp",EDGE,"E26"),sQuery(id+"F12.wireOp",EDGE,"E27"),sQuery(id+"F12.wireOp",EDGE,"E28"),sQuery(id+"F12.wireOp",EDGE,"E29"),sQuery(id+"F12.wireOp",EDGE,"E30"),sQuery(id+"F12.wireOp",EDGE,"E31"),sQuery(id+"F12.wireOp",EDGE,"E32"),sQuery(id+"F12.wireOp",EDGE,"E33"),sQuery(id+"F12.wireOp",EDGE,"E34"),sQuery(id+"F12.wireOp",EDGE,"E35"),sQuery(id+"F12.wireOp",EDGE,"E36"),sQuery(id+"F12.wireOp",EDGE,"E37"),sQuery(id+"F12.wireOp",EDGE,"E38"),sQuery(id+"F12.wireOp",EDGE,"E39"),sQuery(id+"F12.wireOp",EDGE,"E40"),sQuery(id+"F12.wireOp",EDGE,"E41"),sQuery(id+"F12.wireOp",EDGE,"E42"),sQuery(id+"F12.wireOp",EDGE,"E43"),sQuery(id+"F12.wireOp",EDGE,"E44"),sQuery(id+"F12.wireOp",EDGE,"E45"),sQuery(id+"F12.wireOp",EDGE,"E46"),sQuery(id+"F12.wireOp",EDGE,"E47"),sQuery(id+"F12.wireOp",EDGE,"E48"),sQuery(id+"F12.wireOp",EDGE,"E49"),sQuery(id+"F12.wireOp",EDGE,"E50"),sQuery(id+"F12.wireOp",EDGE,"E51"),sQuery(id+"F12.wireOp",EDGE,"E52"),sQuery(id+"F12.wireOp",EDGE,"E53"),sQuery(id+"F12.wireOp",EDGE,"E54"),sQuery(id+"F12.wireOp",EDGE,"E55"),sQuery(id+"F12.wireOp",EDGE,"E56"),sQuery(id+"F12.wireOp",EDGE,"E57"),sQuery(id+"F12.wireOp",EDGE,"E58"),sQuery(id+"F12.wireOp",EDGE,"E59"),sQuery(id+"F12.wireOp",EDGE,"E60"),sQuery(id+"F12.wireOp",EDGE,"E61"),sQuery(id+"F12.wireOp",EDGE,"E62"),sQuery(id+"F12.wireOp",EDGE,"E63"),sQuery(id+"F12.wireOp",EDGE,"E64"),sQuery(id+"F12.wireOp",EDGE,"E65"),sQuery(id+"F12.wireOp",EDGE,"E66"),sQuery(id+"F12.wireOp",EDGE,"E67"),sQuery(id+"F12.wireOp",EDGE,"E68"),sQuery(id+"F12.wireOp",EDGE,"E69"),sQuery(id+"F12.wireOp",EDGE,"E70"),sQuery(id+"F12.wireOp",EDGE,"E71"),sQuery(id+"F12.wireOp",EDGE,"E72"),sQuery(id+"F12.wireOp",EDGE,"E73"),sQuery(id+"F12.wireOp",EDGE,"E74"),sQuery(id+"F12.wireOp",EDGE,"E75"),sQuery(id+"F12.wireOp",EDGE,"E76"),sQuery(id+"F12.wireOp",EDGE,"E77"),sQuery(id+"F12.wireOp",EDGE,"E78"),sQuery(id+"F12.wireOp",EDGE,"E79"),sQuery(id+"F12.wireOp",EDGE,"E80"),sQuery(id+"F12.wireOp",EDGE,"E81"),sQuery(id+"F12.wireOp",EDGE,"E82")])],"isStart":false})});
            extrude(context, id + "F15", {"entities" : qUnion([Q0]), "operationType" : NewBodyOperationType.ADD, "oppositeDirection" : true, "depth" : 25.4 * mm, "offsetDistance" : 25.4 * mm});
        }
        {
            var Q0;
            Q0=makeQuery(id+"F15.opExtrude","CAP_FACE",FACE,{"disambiguationData":[OSD([sQuery(id+"F12.wireOp",EDGE,"E23"),sQuery(id+"F12.wireOp",EDGE,"E24"),sQuery(id+"F12.wireOp",EDGE,"E25"),sQuery(id+"F12.wireOp",EDGE,"E26"),sQuery(id+"F12.wireOp",EDGE,"E27"),sQuery(id+"F12.wireOp",EDGE,"E28"),sQuery(id+"F12.wireOp",EDGE,"E29"),sQuery(id+"F12.wireOp",EDGE,"E30"),sQuery(id+"F12.wireOp",EDGE,"E31"),sQuery(id+"F12.wireOp",EDGE,"E32"),sQuery(id+"F12.wireOp",EDGE,"E33"),sQuery(id+"F12.wireOp",EDGE,"E34"),sQuery(id+"F12.wireOp",EDGE,"E35"),sQuery(id+"F12.wireOp",EDGE,"E36"),sQuery(id+"F12.wireOp",EDGE,"E37"),sQuery(id+"F12.wireOp",EDGE,"E38"),sQuery(id+"F12.wireOp",EDGE,"E39"),sQuery(id+"F12.wireOp",EDGE,"E40"),sQuery(id+"F12.wireOp",EDGE,"E41"),sQuery(id+"F12.wireOp",EDGE,"E42"),sQuery(id+"F12.wireOp",EDGE,"E43"),sQuery(id+"F12.wireOp",EDGE,"E44"),sQuery(id+"F12.wireOp",EDGE,"E45"),sQuery(id+"F12.wireOp",EDGE,"E46"),sQuery(id+"F12.wireOp",EDGE,"E47"),sQuery(id+"F12.wireOp",EDGE,"E48"),sQuery(id+"F12.wireOp",EDGE,"E49"),sQuery(id+"F12.wireOp",EDGE,"E50"),sQuery(id+"F12.wireOp",EDGE,"E51"),sQuery(id+"F12.wireOp",EDGE,"E52"),sQuery(id+"F12.wireOp",EDGE,"E53"),sQuery(id+"F12.wireOp",EDGE,"E54"),sQuery(id+"F12.wireOp",EDGE,"E55"),sQuery(id+"F12.wireOp",EDGE,"E56"),sQuery(id+"F12.wireOp",EDGE,"E57"),sQuery(id+"F12.wireOp",EDGE,"E58"),sQuery(id+"F12.wireOp",EDGE,"E59"),sQuery(id+"F12.wireOp",EDGE,"E60"),sQuery(id+"F12.wireOp",EDGE,"E61"),sQuery(id+"F12.wireOp",EDGE,"E62"),sQuery(id+"F12.wireOp",EDGE,"E63"),sQuery(id+"F12.wireOp",EDGE,"E64"),sQuery(id+"F12.wireOp",EDGE,"E65"),sQuery(id+"F12.wireOp",EDGE,"E66"),sQuery(id+"F12.wireOp",EDGE,"E67"),sQuery(id+"F12.wireOp",EDGE,"E68"),sQuery(id+"F12.wireOp",EDGE,"E69"),sQuery(id+"F12.wireOp",EDGE,"E70"),sQuery(id+"F12.wireOp",EDGE,"E71"),sQuery(id+"F12.wireOp",EDGE,"E72"),sQuery(id+"F12.wireOp",EDGE,"E73"),sQuery(id+"F12.wireOp",EDGE,"E74"),sQuery(id+"F12.wireOp",EDGE,"E75"),sQuery(id+"F12.wireOp",EDGE,"E76"),sQuery(id+"F12.wireOp",EDGE,"E77"),sQuery(id+"F12.wireOp",EDGE,"E78"),sQuery(id+"F12.wireOp",EDGE,"E79"),sQuery(id+"F12.wireOp",EDGE,"E80"),sQuery(id+"F12.wireOp",EDGE,"E81"),sQuery(id+"F12.wireOp",EDGE,"E82")])],"isStart":false});
            extrude(context, id + "F16", {"entities" : qUnion([Q0]), "operationType" : NewBodyOperationType.REMOVE, "oppositeDirection" : true, "depth" : 6.35 * mm, "offsetDistance" : 25.4 * mm});
        }
        {
            var Q0;
            Q0=makeQuery(id+"F14.boolean.opBoolean","COPY",FACE,{"derivedFrom":makeQuery(id+"F14.opExtrude","CAP_FACE",FACE,{"disambiguationData":[OSD([sQuery(id+"F12.wireOp",EDGE,"E23"),sQuery(id+"F12.wireOp",EDGE,"E24"),sQuery(id+"F12.wireOp",EDGE,"E25"),sQuery(id+"F12.wireOp",EDGE,"E26"),sQuery(id+"F12.wireOp",EDGE,"E27"),sQuery(id+"F12.wireOp",EDGE,"E28"),sQuery(id+"F12.wireOp",EDGE,"E29"),sQuery(id+"F12.wireOp",EDGE,"E30"),sQuery(id+"F12.wireOp",EDGE,"E31"),sQuery(id+"F12.wireOp",EDGE,"E32"),sQuery(id+"F12.wireOp",EDGE,"E33"),sQuery(id+"F12.wireOp",EDGE,"E34"),sQuery(id+"F12.wireOp",EDGE,"E35"),sQuery(id+"F12.wireOp",EDGE,"E36"),sQuery(id+"F12.wireOp",EDGE,"E37"),sQuery(id+"F12.wireOp",EDGE,"E38"),sQuery(id+"F12.wireOp",EDGE,"E39"),sQuery(id+"F12.wireOp",EDGE,"E40"),sQuery(id+"F12.wireOp",EDGE,"E41"),sQuery(id+"F12.wireOp",EDGE,"E42"),sQuery(id+"F12.wireOp",EDGE,"E43"),sQuery(id+"F12.wireOp",EDGE,"E44"),sQuery(id+"F12.wireOp",EDGE,"E45"),sQuery(id+"F12.wireOp",EDGE,"E46"),sQuery(id+"F12.wireOp",EDGE,"E47"),sQuery(id+"F12.wireOp",EDGE,"E48"),sQuery(id+"F12.wireOp",EDGE,"E49"),sQuery(id+"F12.wireOp",EDGE,"E50"),sQuery(id+"F12.wireOp",EDGE,"E51"),sQuery(id+"F12.wireOp",EDGE,"E52"),sQuery(id+"F12.wireOp",EDGE,"E53"),sQuery(id+"F12.wireOp",EDGE,"E54"),sQuery(id+"F12.wireOp",EDGE,"E55"),sQuery(id+"F12.wireOp",EDGE,"E56"),sQuery(id+"F12.wireOp",EDGE,"E57"),sQuery(id+"F12.wireOp",EDGE,"E58"),sQuery(id+"F12.wireOp",EDGE,"E59"),sQuery(id+"F12.wireOp",EDGE,"E60"),sQuery(id+"F12.wireOp",EDGE,"E61"),sQuery(id+"F12.wireOp",EDGE,"E62"),sQuery(id+"F12.wireOp",EDGE,"E63"),sQuery(id+"F12.wireOp",EDGE,"E64"),sQuery(id+"F12.wireOp",EDGE,"E65"),sQuery(id+"F12.wireOp",EDGE,"E66"),sQuery(id+"F12.wireOp",EDGE,"E67"),sQuery(id+"F12.wireOp",EDGE,"E68"),sQuery(id+"F12.wireOp",EDGE,"E69"),sQuery(id+"F12.wireOp",EDGE,"E70"),sQuery(id+"F12.wireOp",EDGE,"E71"),sQuery(id+"F12.wireOp",EDGE,"E72"),sQuery(id+"F12.wireOp",EDGE,"E73"),sQuery(id+"F12.wireOp",EDGE,"E74"),sQuery(id+"F12.wireOp",EDGE,"E75"),sQuery(id+"F12.wireOp",EDGE,"E76"),sQuery(id+"F12.wireOp",EDGE,"E77"),sQuery(id+"F12.wireOp",EDGE,"E78"),sQuery(id+"F12.wireOp",EDGE,"E79"),sQuery(id+"F12.wireOp",EDGE,"E80"),sQuery(id+"F12.wireOp",EDGE,"E81"),sQuery(id+"F12.wireOp",EDGE,"E82")])],"isStart":false})});
            extrude(context, id + "F17", {"entities" : qUnion([Q0]), "operationType" : NewBodyOperationType.REMOVE, "oppositeDirection" : true, "depth" : 3.05 * mm, "offsetDistance" : 25.4 * mm});
        }
        {
            var Q0;
            Q0=makeQuery(id+"F17.boolean.opBoolean","COPY",FACE,{"derivedFrom":makeQuery(id+"F17.opExtrude","CAP_FACE",FACE,{"disambiguationData":[OSD([sQuery(id+"F12.wireOp",EDGE,"E23"),sQuery(id+"F12.wireOp",EDGE,"E24"),sQuery(id+"F12.wireOp",EDGE,"E25"),sQuery(id+"F12.wireOp",EDGE,"E26"),sQuery(id+"F12.wireOp",EDGE,"E27"),sQuery(id+"F12.wireOp",EDGE,"E28"),sQuery(id+"F12.wireOp",EDGE,"E29"),sQuery(id+"F12.wireOp",EDGE,"E30"),sQuery(id+"F12.wireOp",EDGE,"E31"),sQuery(id+"F12.wireOp",EDGE,"E32"),sQuery(id+"F12.wireOp",EDGE,"E33"),sQuery(id+"F12.wireOp",EDGE,"E34"),sQuery(id+"F12.wireOp",EDGE,"E35"),sQuery(id+"F12.wireOp",EDGE,"E36"),sQuery(id+"F12.wireOp",EDGE,"E37"),sQuery(id+"F12.wireOp",EDGE,"E38"),sQuery(id+"F12.wireOp",EDGE,"E39"),sQuery(id+"F12.wireOp",EDGE,"E40"),sQuery(id+"F12.wireOp",EDGE,"E41"),sQuery(id+"F12.wireOp",EDGE,"E42"),sQuery(id+"F12.wireOp",EDGE,"E43"),sQuery(id+"F12.wireOp",EDGE,"E44"),sQuery(id+"F12.wireOp",EDGE,"E45"),sQuery(id+"F12.wireOp",EDGE,"E46"),sQuery(id+"F12.wireOp",EDGE,"E47"),sQuery(id+"F12.wireOp",EDGE,"E48"),sQuery(id+"F12.wireOp",EDGE,"E49"),sQuery(id+"F12.wireOp",EDGE,"E50"),sQuery(id+"F12.wireOp",EDGE,"E51"),sQuery(id+"F12.wireOp",EDGE,"E52"),sQuery(id+"F12.wireOp",EDGE,"E53"),sQuery(id+"F12.wireOp",EDGE,"E54"),sQuery(id+"F12.wireOp",EDGE,"E55"),sQuery(id+"F12.wireOp",EDGE,"E56"),sQuery(id+"F12.wireOp",EDGE,"E57"),sQuery(id+"F12.wireOp",EDGE,"E58"),sQuery(id+"F12.wireOp",EDGE,"E59"),sQuery(id+"F12.wireOp",EDGE,"E60"),sQuery(id+"F12.wireOp",EDGE,"E61"),sQuery(id+"F12.wireOp",EDGE,"E62"),sQuery(id+"F12.wireOp",EDGE,"E63"),sQuery(id+"F12.wireOp",EDGE,"E64"),sQuery(id+"F12.wireOp",EDGE,"E65"),sQuery(id+"F12.wireOp",EDGE,"E66"),sQuery(id+"F12.wireOp",EDGE,"E67"),sQuery(id+"F12.wireOp",EDGE,"E68"),sQuery(id+"F12.wireOp",EDGE,"E69"),sQuery(id+"F12.wireOp",EDGE,"E70"),sQuery(id+"F12.wireOp",EDGE,"E71"),sQuery(id+"F12.wireOp",EDGE,"E72"),sQuery(id+"F12.wireOp",EDGE,"E73"),sQuery(id+"F12.wireOp",EDGE,"E74"),sQuery(id+"F12.wireOp",EDGE,"E75"),sQuery(id+"F12.wireOp",EDGE,"E76"),sQuery(id+"F12.wireOp",EDGE,"E77"),sQuery(id+"F12.wireOp",EDGE,"E78"),sQuery(id+"F12.wireOp",EDGE,"E79"),sQuery(id+"F12.wireOp",EDGE,"E80"),sQuery(id+"F12.wireOp",EDGE,"E81"),sQuery(id+"F12.wireOp",EDGE,"E82")])],"isStart":false})});
            extrude(context, id + "F18", {"entities" : qUnion([Q0]), "operationType" : NewBodyOperationType.REMOVE, "oppositeDirection" : true, "depth" : 0.25 * mm, "offsetDistance" : 25.4 * mm});
        }
        {
            var Q0;
            Q0=makeQuery(id+"F11.opExtrude","CAP_EDGE",EDGE,{"disambiguationData":[OSD([sQuery(id+"F0.wireOp",EDGE,"E6")])],"isStart":false});
            var Q1;
            Q1=makeQuery(id+"F9.boolean.opBoolean","COPY",EDGE,{"derivedFrom":makeQuery(id+"F9.opExtrude","CAP_EDGE",EDGE,{"disambiguationData":[OSD([sQuery(id+"F0.wireOp",EDGE,"E6")])],"isStart":false})});
            var Q2;
            Q2=makeQuery(id+"F11.opExtrude","CAP_EDGE",EDGE,{"disambiguationData":[OSD([sQuery(id+"F0.wireOp",EDGE,"E5")])],"isStart":false});
            var Q3;
            Q3=makeQuery(id+"F9.boolean.opBoolean","COPY",EDGE,{"derivedFrom":makeQuery(id+"F9.opExtrude","CAP_EDGE",EDGE,{"disambiguationData":[OSD([sQuery(id+"F0.wireOp",EDGE,"E5")])],"isStart":false})});
            chamfer(context, id + "F19", {"entities" : qUnion([Q0, Q1, Q2, Q3]), "width" : 8.38 * mm, "tangentPropagation" : true});
        }
        {
            var Q0;
            Q0=makeQuery(id+"F15.boolean.opBoolean","SPLIT",FACE,{"disambiguationData":[TD([makeQuery(id+"F15.opExtrude","SWEPT_FACE",FACE,{"disambiguationData":[OSD([sQuery(id+"F12.wireOp",EDGE,"E50")])]})])],"derivedFrom":makeQuery(id+"F11.opExtrude","CAP_FACE",FACE,{"disambiguationData":[OSD([sQuery(id+"F0.wireOp",EDGE,"E1"),sQuery(id+"F0.wireOp",EDGE,"E5"),sQuery(id+"F0.wireOp",EDGE,"E6"),sQuery(id+"F3.wireOp",EDGE,"E13"),sQuery(id+"F3.wireOp",EDGE,"E14"),sQuery(id+"F3.wireOp",EDGE,"E15"),sQuery(id+"F3.wireOp",EDGE,"E16"),sQuery(id+"F3.wireOp",EDGE,"E17"),sQuery(id+"F3.wireOp",EDGE,"E18"),sQuery(id+"F3.wireOp",EDGE,"E19"),sQuery(id+"F3.wireOp",EDGE,"E20"),sQuery(id+"F3.wireOp",EDGE,"E21"),sQuery(id+"F3.wireOp",EDGE,"E22")])],"isStart":false})});
            var Q1;
            Q1=makeQuery(id+"F15.boolean.opBoolean","SPLIT",FACE,{"disambiguationData":[TD([makeQuery(id+"F15.opExtrude","SWEPT_FACE",FACE,{"disambiguationData":[OSD([sQuery(id+"F12.wireOp",EDGE,"E53")])]})])],"derivedFrom":makeQuery(id+"F11.opExtrude","CAP_FACE",FACE,{"disambiguationData":[OSD([sQuery(id+"F0.wireOp",EDGE,"E1"),sQuery(id+"F0.wireOp",EDGE,"E5"),sQuery(id+"F0.wireOp",EDGE,"E6"),sQuery(id+"F3.wireOp",EDGE,"E13"),sQuery(id+"F3.wireOp",EDGE,"E14"),sQuery(id+"F3.wireOp",EDGE,"E15"),sQuery(id+"F3.wireOp",EDGE,"E16"),sQuery(id+"F3.wireOp",EDGE,"E17"),sQuery(id+"F3.wireOp",EDGE,"E18"),sQuery(id+"F3.wireOp",EDGE,"E19"),sQuery(id+"F3.wireOp",EDGE,"E20"),sQuery(id+"F3.wireOp",EDGE,"E21"),sQuery(id+"F3.wireOp",EDGE,"E22")])],"isStart":false})});
            var Q2;
            Q2=makeQuery(id+"F15.boolean.opBoolean","SPLIT",FACE,{"disambiguationData":[TD([makeQuery(id+"F15.opExtrude","SWEPT_FACE",FACE,{"disambiguationData":[OSD([sQuery(id+"F12.wireOp",EDGE,"E47")])]})])],"derivedFrom":makeQuery(id+"F11.opExtrude","CAP_FACE",FACE,{"disambiguationData":[OSD([sQuery(id+"F0.wireOp",EDGE,"E1"),sQuery(id+"F0.wireOp",EDGE,"E5"),sQuery(id+"F0.wireOp",EDGE,"E6"),sQuery(id+"F3.wireOp",EDGE,"E13"),sQuery(id+"F3.wireOp",EDGE,"E14"),sQuery(id+"F3.wireOp",EDGE,"E15"),sQuery(id+"F3.wireOp",EDGE,"E16"),sQuery(id+"F3.wireOp",EDGE,"E17"),sQuery(id+"F3.wireOp",EDGE,"E18"),sQuery(id+"F3.wireOp",EDGE,"E19"),sQuery(id+"F3.wireOp",EDGE,"E20"),sQuery(id+"F3.wireOp",EDGE,"E21"),sQuery(id+"F3.wireOp",EDGE,"E22")])],"isStart":false})});
            var Q3;
            Q3=makeQuery(id+"F15.boolean.opBoolean","SPLIT",FACE,{"disambiguationData":[TD([makeQuery(id+"F15.opExtrude","SWEPT_FACE",FACE,{"disambiguationData":[OSD([sQuery(id+"F12.wireOp",EDGE,"E36")])]})])],"derivedFrom":makeQuery(id+"F11.opExtrude","CAP_FACE",FACE,{"disambiguationData":[OSD([sQuery(id+"F0.wireOp",EDGE,"E1"),sQuery(id+"F0.wireOp",EDGE,"E5"),sQuery(id+"F0.wireOp",EDGE,"E6"),sQuery(id+"F3.wireOp",EDGE,"E13"),sQuery(id+"F3.wireOp",EDGE,"E14"),sQuery(id+"F3.wireOp",EDGE,"E15"),sQuery(id+"F3.wireOp",EDGE,"E16"),sQuery(id+"F3.wireOp",EDGE,"E17"),sQuery(id+"F3.wireOp",EDGE,"E18"),sQuery(id+"F3.wireOp",EDGE,"E19"),sQuery(id+"F3.wireOp",EDGE,"E20"),sQuery(id+"F3.wireOp",EDGE,"E21"),sQuery(id+"F3.wireOp",EDGE,"E22")])],"isStart":false})});
            var Q4;
            Q4=makeQuery(id+"F15.boolean.opBoolean","SPLIT",FACE,{"disambiguationData":[TD([makeQuery(id+"F15.opExtrude","SWEPT_FACE",FACE,{"disambiguationData":[OSD([sQuery(id+"F12.wireOp",EDGE,"E41")])]})])],"derivedFrom":makeQuery(id+"F11.opExtrude","CAP_FACE",FACE,{"disambiguationData":[OSD([sQuery(id+"F0.wireOp",EDGE,"E1"),sQuery(id+"F0.wireOp",EDGE,"E5"),sQuery(id+"F0.wireOp",EDGE,"E6"),sQuery(id+"F3.wireOp",EDGE,"E13"),sQuery(id+"F3.wireOp",EDGE,"E14"),sQuery(id+"F3.wireOp",EDGE,"E15"),sQuery(id+"F3.wireOp",EDGE,"E16"),sQuery(id+"F3.wireOp",EDGE,"E17"),sQuery(id+"F3.wireOp",EDGE,"E18"),sQuery(id+"F3.wireOp",EDGE,"E19"),sQuery(id+"F3.wireOp",EDGE,"E20"),sQuery(id+"F3.wireOp",EDGE,"E21"),sQuery(id+"F3.wireOp",EDGE,"E22")])],"isStart":false})});
            var Q5;
            Q5=makeQuery(id+"F15.boolean.opBoolean","SPLIT",FACE,{"disambiguationData":[TD([makeQuery(id+"F15.opExtrude","SWEPT_FACE",FACE,{"disambiguationData":[OSD([sQuery(id+"F12.wireOp",EDGE,"E33")])]})])],"derivedFrom":makeQuery(id+"F11.opExtrude","CAP_FACE",FACE,{"disambiguationData":[OSD([sQuery(id+"F0.wireOp",EDGE,"E1"),sQuery(id+"F0.wireOp",EDGE,"E5"),sQuery(id+"F0.wireOp",EDGE,"E6"),sQuery(id+"F3.wireOp",EDGE,"E13"),sQuery(id+"F3.wireOp",EDGE,"E14"),sQuery(id+"F3.wireOp",EDGE,"E15"),sQuery(id+"F3.wireOp",EDGE,"E16"),sQuery(id+"F3.wireOp",EDGE,"E17"),sQuery(id+"F3.wireOp",EDGE,"E18"),sQuery(id+"F3.wireOp",EDGE,"E19"),sQuery(id+"F3.wireOp",EDGE,"E20"),sQuery(id+"F3.wireOp",EDGE,"E21"),sQuery(id+"F3.wireOp",EDGE,"E22")])],"isStart":false})});
            var Q6;
            Q6=makeQuery(id+"F15.boolean.opBoolean","INTERSECT",EDGE,{"derivedFrom":[makeQuery(id+"F11.opExtrude","CAP_FACE",FACE,{"disambiguationData":[OSD([sQuery(id+"F0.wireOp",EDGE,"E1"),sQuery(id+"F0.wireOp",EDGE,"E5"),sQuery(id+"F0.wireOp",EDGE,"E6"),sQuery(id+"F3.wireOp",EDGE,"E13"),sQuery(id+"F3.wireOp",EDGE,"E14"),sQuery(id+"F3.wireOp",EDGE,"E15"),sQuery(id+"F3.wireOp",EDGE,"E16"),sQuery(id+"F3.wireOp",EDGE,"E17"),sQuery(id+"F3.wireOp",EDGE,"E18"),sQuery(id+"F3.wireOp",EDGE,"E19"),sQuery(id+"F3.wireOp",EDGE,"E20"),sQuery(id+"F3.wireOp",EDGE,"E21"),sQuery(id+"F3.wireOp",EDGE,"E22")])],"isStart":false}),makeQuery(id+"F15.opExtrude","SWEPT_FACE",FACE,{"disambiguationData":[OSD([sQuery(id+"F12.wireOp",EDGE,"E23")])]})]});
            var Q7;
            Q7=makeQuery(id+"F15.boolean.opBoolean","INTERSECT",EDGE,{"derivedFrom":[makeQuery(id+"F11.opExtrude","CAP_FACE",FACE,{"disambiguationData":[OSD([sQuery(id+"F0.wireOp",EDGE,"E1"),sQuery(id+"F0.wireOp",EDGE,"E5"),sQuery(id+"F0.wireOp",EDGE,"E6"),sQuery(id+"F3.wireOp",EDGE,"E13"),sQuery(id+"F3.wireOp",EDGE,"E14"),sQuery(id+"F3.wireOp",EDGE,"E15"),sQuery(id+"F3.wireOp",EDGE,"E16"),sQuery(id+"F3.wireOp",EDGE,"E17"),sQuery(id+"F3.wireOp",EDGE,"E18"),sQuery(id+"F3.wireOp",EDGE,"E19"),sQuery(id+"F3.wireOp",EDGE,"E20"),sQuery(id+"F3.wireOp",EDGE,"E21"),sQuery(id+"F3.wireOp",EDGE,"E22")])],"isStart":false}),makeQuery(id+"F15.opExtrude","SWEPT_FACE",FACE,{"disambiguationData":[OSD([sQuery(id+"F12.wireOp",EDGE,"E58")])]})]});
            var Q8;
            Q8=makeQuery(id+"F15.boolean.opBoolean","INTERSECT",EDGE,{"derivedFrom":[makeQuery(id+"F11.opExtrude","CAP_FACE",FACE,{"disambiguationData":[OSD([sQuery(id+"F0.wireOp",EDGE,"E1"),sQuery(id+"F0.wireOp",EDGE,"E5"),sQuery(id+"F0.wireOp",EDGE,"E6"),sQuery(id+"F3.wireOp",EDGE,"E13"),sQuery(id+"F3.wireOp",EDGE,"E14"),sQuery(id+"F3.wireOp",EDGE,"E15"),sQuery(id+"F3.wireOp",EDGE,"E16"),sQuery(id+"F3.wireOp",EDGE,"E17"),sQuery(id+"F3.wireOp",EDGE,"E18"),sQuery(id+"F3.wireOp",EDGE,"E19"),sQuery(id+"F3.wireOp",EDGE,"E20"),sQuery(id+"F3.wireOp",EDGE,"E21"),sQuery(id+"F3.wireOp",EDGE,"E22")])],"isStart":false}),makeQuery(id+"F15.opExtrude","SWEPT_FACE",FACE,{"disambiguationData":[OSD([sQuery(id+"F12.wireOp",EDGE,"E30")])]})]});
            var Q9;
            Q9=makeQuery(id+"F15.boolean.opBoolean","INTERSECT",EDGE,{"derivedFrom":[makeQuery(id+"F11.opExtrude","CAP_FACE",FACE,{"disambiguationData":[OSD([sQuery(id+"F0.wireOp",EDGE,"E1"),sQuery(id+"F0.wireOp",EDGE,"E5"),sQuery(id+"F0.wireOp",EDGE,"E6"),sQuery(id+"F3.wireOp",EDGE,"E13"),sQuery(id+"F3.wireOp",EDGE,"E14"),sQuery(id+"F3.wireOp",EDGE,"E15"),sQuery(id+"F3.wireOp",EDGE,"E16"),sQuery(id+"F3.wireOp",EDGE,"E17"),sQuery(id+"F3.wireOp",EDGE,"E18"),sQuery(id+"F3.wireOp",EDGE,"E19"),sQuery(id+"F3.wireOp",EDGE,"E20"),sQuery(id+"F3.wireOp",EDGE,"E21"),sQuery(id+"F3.wireOp",EDGE,"E22")])],"isStart":false}),makeQuery(id+"F15.opExtrude","SWEPT_FACE",FACE,{"disambiguationData":[OSD([sQuery(id+"F12.wireOp",EDGE,"E31")])]})]});
            var Q10;
            Q10=makeQuery(id+"F15.boolean.opBoolean","INTERSECT",EDGE,{"derivedFrom":[makeQuery(id+"F11.opExtrude","CAP_FACE",FACE,{"disambiguationData":[OSD([sQuery(id+"F0.wireOp",EDGE,"E1"),sQuery(id+"F0.wireOp",EDGE,"E5"),sQuery(id+"F0.wireOp",EDGE,"E6"),sQuery(id+"F3.wireOp",EDGE,"E13"),sQuery(id+"F3.wireOp",EDGE,"E14"),sQuery(id+"F3.wireOp",EDGE,"E15"),sQuery(id+"F3.wireOp",EDGE,"E16"),sQuery(id+"F3.wireOp",EDGE,"E17"),sQuery(id+"F3.wireOp",EDGE,"E18"),sQuery(id+"F3.wireOp",EDGE,"E19"),sQuery(id+"F3.wireOp",EDGE,"E20"),sQuery(id+"F3.wireOp",EDGE,"E21"),sQuery(id+"F3.wireOp",EDGE,"E22")])],"isStart":false}),makeQuery(id+"F15.opExtrude","SWEPT_FACE",FACE,{"disambiguationData":[OSD([sQuery(id+"F12.wireOp",EDGE,"E57")])]})]});
            var Q11;
            Q11=makeQuery(id+"F15.boolean.opBoolean","INTERSECT",EDGE,{"derivedFrom":[makeQuery(id+"F11.opExtrude","CAP_FACE",FACE,{"disambiguationData":[OSD([sQuery(id+"F0.wireOp",EDGE,"E1"),sQuery(id+"F0.wireOp",EDGE,"E5"),sQuery(id+"F0.wireOp",EDGE,"E6"),sQuery(id+"F3.wireOp",EDGE,"E13"),sQuery(id+"F3.wireOp",EDGE,"E14"),sQuery(id+"F3.wireOp",EDGE,"E15"),sQuery(id+"F3.wireOp",EDGE,"E16"),sQuery(id+"F3.wireOp",EDGE,"E17"),sQuery(id+"F3.wireOp",EDGE,"E18"),sQuery(id+"F3.wireOp",EDGE,"E19"),sQuery(id+"F3.wireOp",EDGE,"E20"),sQuery(id+"F3.wireOp",EDGE,"E21"),sQuery(id+"F3.wireOp",EDGE,"E22")])],"isStart":false}),makeQuery(id+"F15.opExtrude","SWEPT_FACE",FACE,{"disambiguationData":[OSD([sQuery(id+"F12.wireOp",EDGE,"E29")])]})]});
            var Q12;
            Q12=makeQuery(id+"F15.boolean.opBoolean","INTERSECT",EDGE,{"derivedFrom":[makeQuery(id+"F11.opExtrude","CAP_FACE",FACE,{"disambiguationData":[OSD([sQuery(id+"F0.wireOp",EDGE,"E1"),sQuery(id+"F0.wireOp",EDGE,"E5"),sQuery(id+"F0.wireOp",EDGE,"E6"),sQuery(id+"F3.wireOp",EDGE,"E13"),sQuery(id+"F3.wireOp",EDGE,"E14"),sQuery(id+"F3.wireOp",EDGE,"E15"),sQuery(id+"F3.wireOp",EDGE,"E16"),sQuery(id+"F3.wireOp",EDGE,"E17"),sQuery(id+"F3.wireOp",EDGE,"E18"),sQuery(id+"F3.wireOp",EDGE,"E19"),sQuery(id+"F3.wireOp",EDGE,"E20"),sQuery(id+"F3.wireOp",EDGE,"E21"),sQuery(id+"F3.wireOp",EDGE,"E22")])],"isStart":false}),makeQuery(id+"F15.opExtrude","SWEPT_FACE",FACE,{"disambiguationData":[OSD([sQuery(id+"F12.wireOp",EDGE,"E80")])]})]});
            var Q13;
            Q13=makeQuery(id+"F15.boolean.opBoolean","INTERSECT",EDGE,{"derivedFrom":[makeQuery(id+"F11.opExtrude","CAP_FACE",FACE,{"disambiguationData":[OSD([sQuery(id+"F0.wireOp",EDGE,"E1"),sQuery(id+"F0.wireOp",EDGE,"E5"),sQuery(id+"F0.wireOp",EDGE,"E6"),sQuery(id+"F3.wireOp",EDGE,"E13"),sQuery(id+"F3.wireOp",EDGE,"E14"),sQuery(id+"F3.wireOp",EDGE,"E15"),sQuery(id+"F3.wireOp",EDGE,"E16"),sQuery(id+"F3.wireOp",EDGE,"E17"),sQuery(id+"F3.wireOp",EDGE,"E18"),sQuery(id+"F3.wireOp",EDGE,"E19"),sQuery(id+"F3.wireOp",EDGE,"E20"),sQuery(id+"F3.wireOp",EDGE,"E21"),sQuery(id+"F3.wireOp",EDGE,"E22")])],"isStart":false}),makeQuery(id+"F15.opExtrude","SWEPT_FACE",FACE,{"disambiguationData":[OSD([sQuery(id+"F12.wireOp",EDGE,"E39")])]})]});
            var Q14;
            Q14=makeQuery(id+"F15.boolean.opBoolean","INTERSECT",EDGE,{"derivedFrom":[makeQuery(id+"F11.opExtrude","CAP_FACE",FACE,{"disambiguationData":[OSD([sQuery(id+"F0.wireOp",EDGE,"E1"),sQuery(id+"F0.wireOp",EDGE,"E5"),sQuery(id+"F0.wireOp",EDGE,"E6"),sQuery(id+"F3.wireOp",EDGE,"E13"),sQuery(id+"F3.wireOp",EDGE,"E14"),sQuery(id+"F3.wireOp",EDGE,"E15"),sQuery(id+"F3.wireOp",EDGE,"E16"),sQuery(id+"F3.wireOp",EDGE,"E17"),sQuery(id+"F3.wireOp",EDGE,"E18"),sQuery(id+"F3.wireOp",EDGE,"E19"),sQuery(id+"F3.wireOp",EDGE,"E20"),sQuery(id+"F3.wireOp",EDGE,"E21"),sQuery(id+"F3.wireOp",EDGE,"E22")])],"isStart":false}),makeQuery(id+"F15.opExtrude","SWEPT_FACE",FACE,{"disambiguationData":[OSD([sQuery(id+"F12.wireOp",EDGE,"E78")])]})]});
            var Q15;
            Q15=makeQuery(id+"F15.boolean.opBoolean","INTERSECT",EDGE,{"derivedFrom":[makeQuery(id+"F11.opExtrude","CAP_FACE",FACE,{"disambiguationData":[OSD([sQuery(id+"F0.wireOp",EDGE,"E1"),sQuery(id+"F0.wireOp",EDGE,"E5"),sQuery(id+"F0.wireOp",EDGE,"E6"),sQuery(id+"F3.wireOp",EDGE,"E13"),sQuery(id+"F3.wireOp",EDGE,"E14"),sQuery(id+"F3.wireOp",EDGE,"E15"),sQuery(id+"F3.wireOp",EDGE,"E16"),sQuery(id+"F3.wireOp",EDGE,"E17"),sQuery(id+"F3.wireOp",EDGE,"E18"),sQuery(id+"F3.wireOp",EDGE,"E19"),sQuery(id+"F3.wireOp",EDGE,"E20"),sQuery(id+"F3.wireOp",EDGE,"E21"),sQuery(id+"F3.wireOp",EDGE,"E22")])],"isStart":false}),makeQuery(id+"F15.opExtrude","SWEPT_FACE",FACE,{"disambiguationData":[OSD([sQuery(id+"F12.wireOp",EDGE,"E75")])]})]});
            var Q16;
            Q16=makeQuery(id+"F15.boolean.opBoolean","INTERSECT",EDGE,{"derivedFrom":[makeQuery(id+"F11.opExtrude","CAP_FACE",FACE,{"disambiguationData":[OSD([sQuery(id+"F0.wireOp",EDGE,"E1"),sQuery(id+"F0.wireOp",EDGE,"E5"),sQuery(id+"F0.wireOp",EDGE,"E6"),sQuery(id+"F3.wireOp",EDGE,"E13"),sQuery(id+"F3.wireOp",EDGE,"E14"),sQuery(id+"F3.wireOp",EDGE,"E15"),sQuery(id+"F3.wireOp",EDGE,"E16"),sQuery(id+"F3.wireOp",EDGE,"E17"),sQuery(id+"F3.wireOp",EDGE,"E18"),sQuery(id+"F3.wireOp",EDGE,"E19"),sQuery(id+"F3.wireOp",EDGE,"E20"),sQuery(id+"F3.wireOp",EDGE,"E21"),sQuery(id+"F3.wireOp",EDGE,"E22")])],"isStart":false}),makeQuery(id+"F15.opExtrude","SWEPT_FACE",FACE,{"disambiguationData":[OSD([sQuery(id+"F12.wireOp",EDGE,"E40")])]})]});
            var Q17;
            Q17=makeQuery(id+"F15.boolean.opBoolean","INTERSECT",EDGE,{"derivedFrom":[makeQuery(id+"F11.opExtrude","CAP_FACE",FACE,{"disambiguationData":[OSD([sQuery(id+"F0.wireOp",EDGE,"E1"),sQuery(id+"F0.wireOp",EDGE,"E5"),sQuery(id+"F0.wireOp",EDGE,"E6"),sQuery(id+"F3.wireOp",EDGE,"E13"),sQuery(id+"F3.wireOp",EDGE,"E14"),sQuery(id+"F3.wireOp",EDGE,"E15"),sQuery(id+"F3.wireOp",EDGE,"E16"),sQuery(id+"F3.wireOp",EDGE,"E17"),sQuery(id+"F3.wireOp",EDGE,"E18"),sQuery(id+"F3.wireOp",EDGE,"E19"),sQuery(id+"F3.wireOp",EDGE,"E20"),sQuery(id+"F3.wireOp",EDGE,"E21"),sQuery(id+"F3.wireOp",EDGE,"E22")])],"isStart":false}),makeQuery(id+"F15.opExtrude","SWEPT_FACE",FACE,{"disambiguationData":[OSD([sQuery(id+"F12.wireOp",EDGE,"E74")])]})]});
            var Q18;
            Q18=makeQuery(id+"F15.boolean.opBoolean","INTERSECT",EDGE,{"derivedFrom":[makeQuery(id+"F11.opExtrude","CAP_FACE",FACE,{"disambiguationData":[OSD([sQuery(id+"F0.wireOp",EDGE,"E1"),sQuery(id+"F0.wireOp",EDGE,"E5"),sQuery(id+"F0.wireOp",EDGE,"E6"),sQuery(id+"F3.wireOp",EDGE,"E13"),sQuery(id+"F3.wireOp",EDGE,"E14"),sQuery(id+"F3.wireOp",EDGE,"E15"),sQuery(id+"F3.wireOp",EDGE,"E16"),sQuery(id+"F3.wireOp",EDGE,"E17"),sQuery(id+"F3.wireOp",EDGE,"E18"),sQuery(id+"F3.wireOp",EDGE,"E19"),sQuery(id+"F3.wireOp",EDGE,"E20"),sQuery(id+"F3.wireOp",EDGE,"E21"),sQuery(id+"F3.wireOp",EDGE,"E22")])],"isStart":false}),makeQuery(id+"F15.opExtrude","SWEPT_FACE",FACE,{"disambiguationData":[OSD([sQuery(id+"F12.wireOp",EDGE,"E28")])]})]});
            var Q19;
            Q19=makeQuery(id+"F15.boolean.opBoolean","INTERSECT",EDGE,{"derivedFrom":[makeQuery(id+"F11.opExtrude","CAP_FACE",FACE,{"disambiguationData":[OSD([sQuery(id+"F0.wireOp",EDGE,"E1"),sQuery(id+"F0.wireOp",EDGE,"E5"),sQuery(id+"F0.wireOp",EDGE,"E6"),sQuery(id+"F3.wireOp",EDGE,"E13"),sQuery(id+"F3.wireOp",EDGE,"E14"),sQuery(id+"F3.wireOp",EDGE,"E15"),sQuery(id+"F3.wireOp",EDGE,"E16"),sQuery(id+"F3.wireOp",EDGE,"E17"),sQuery(id+"F3.wireOp",EDGE,"E18"),sQuery(id+"F3.wireOp",EDGE,"E19"),sQuery(id+"F3.wireOp",EDGE,"E20"),sQuery(id+"F3.wireOp",EDGE,"E21"),sQuery(id+"F3.wireOp",EDGE,"E22")])],"isStart":false}),makeQuery(id+"F15.opExtrude","SWEPT_FACE",FACE,{"disambiguationData":[OSD([sQuery(id+"F12.wireOp",EDGE,"E72")])]})]});
            var Q20;
            Q20=makeQuery(id+"F15.boolean.opBoolean","INTERSECT",EDGE,{"derivedFrom":[makeQuery(id+"F11.opExtrude","CAP_FACE",FACE,{"disambiguationData":[OSD([sQuery(id+"F0.wireOp",EDGE,"E1"),sQuery(id+"F0.wireOp",EDGE,"E5"),sQuery(id+"F0.wireOp",EDGE,"E6"),sQuery(id+"F3.wireOp",EDGE,"E13"),sQuery(id+"F3.wireOp",EDGE,"E14"),sQuery(id+"F3.wireOp",EDGE,"E15"),sQuery(id+"F3.wireOp",EDGE,"E16"),sQuery(id+"F3.wireOp",EDGE,"E17"),sQuery(id+"F3.wireOp",EDGE,"E18"),sQuery(id+"F3.wireOp",EDGE,"E19"),sQuery(id+"F3.wireOp",EDGE,"E20"),sQuery(id+"F3.wireOp",EDGE,"E21"),sQuery(id+"F3.wireOp",EDGE,"E22")])],"isStart":false}),makeQuery(id+"F15.opExtrude","SWEPT_FACE",FACE,{"disambiguationData":[OSD([sQuery(id+"F12.wireOp",EDGE,"E27")])]})]});
            var Q21;
            Q21=makeQuery(id+"F15.boolean.opBoolean","INTERSECT",EDGE,{"derivedFrom":[makeQuery(id+"F11.opExtrude","CAP_FACE",FACE,{"disambiguationData":[OSD([sQuery(id+"F0.wireOp",EDGE,"E1"),sQuery(id+"F0.wireOp",EDGE,"E5"),sQuery(id+"F0.wireOp",EDGE,"E6"),sQuery(id+"F3.wireOp",EDGE,"E13"),sQuery(id+"F3.wireOp",EDGE,"E14"),sQuery(id+"F3.wireOp",EDGE,"E15"),sQuery(id+"F3.wireOp",EDGE,"E16"),sQuery(id+"F3.wireOp",EDGE,"E17"),sQuery(id+"F3.wireOp",EDGE,"E18"),sQuery(id+"F3.wireOp",EDGE,"E19"),sQuery(id+"F3.wireOp",EDGE,"E20"),sQuery(id+"F3.wireOp",EDGE,"E21"),sQuery(id+"F3.wireOp",EDGE,"E22")])],"isStart":false}),makeQuery(id+"F15.opExtrude","SWEPT_FACE",FACE,{"disambiguationData":[OSD([sQuery(id+"F12.wireOp",EDGE,"E26")])]})]});
            var Q22;
            Q22=makeQuery(id+"F15.boolean.opBoolean","INTERSECT",EDGE,{"derivedFrom":[makeQuery(id+"F11.opExtrude","CAP_FACE",FACE,{"disambiguationData":[OSD([sQuery(id+"F0.wireOp",EDGE,"E1"),sQuery(id+"F0.wireOp",EDGE,"E5"),sQuery(id+"F0.wireOp",EDGE,"E6"),sQuery(id+"F3.wireOp",EDGE,"E13"),sQuery(id+"F3.wireOp",EDGE,"E14"),sQuery(id+"F3.wireOp",EDGE,"E15"),sQuery(id+"F3.wireOp",EDGE,"E16"),sQuery(id+"F3.wireOp",EDGE,"E17"),sQuery(id+"F3.wireOp",EDGE,"E18"),sQuery(id+"F3.wireOp",EDGE,"E19"),sQuery(id+"F3.wireOp",EDGE,"E20"),sQuery(id+"F3.wireOp",EDGE,"E21"),sQuery(id+"F3.wireOp",EDGE,"E22")])],"isStart":false}),makeQuery(id+"F15.opExtrude","SWEPT_FACE",FACE,{"disambiguationData":[OSD([sQuery(id+"F12.wireOp",EDGE,"E68")])]})]});
            var Q23;
            Q23=makeQuery(id+"F15.boolean.opBoolean","INTERSECT",EDGE,{"derivedFrom":[makeQuery(id+"F11.opExtrude","CAP_FACE",FACE,{"disambiguationData":[OSD([sQuery(id+"F0.wireOp",EDGE,"E1"),sQuery(id+"F0.wireOp",EDGE,"E5"),sQuery(id+"F0.wireOp",EDGE,"E6"),sQuery(id+"F3.wireOp",EDGE,"E13"),sQuery(id+"F3.wireOp",EDGE,"E14"),sQuery(id+"F3.wireOp",EDGE,"E15"),sQuery(id+"F3.wireOp",EDGE,"E16"),sQuery(id+"F3.wireOp",EDGE,"E17"),sQuery(id+"F3.wireOp",EDGE,"E18"),sQuery(id+"F3.wireOp",EDGE,"E19"),sQuery(id+"F3.wireOp",EDGE,"E20"),sQuery(id+"F3.wireOp",EDGE,"E21"),sQuery(id+"F3.wireOp",EDGE,"E22")])],"isStart":false}),makeQuery(id+"F15.opExtrude","SWEPT_FACE",FACE,{"disambiguationData":[OSD([sQuery(id+"F12.wireOp",EDGE,"E25")])]})]});
            var Q24;
            Q24=makeQuery(id+"F15.boolean.opBoolean","INTERSECT",EDGE,{"derivedFrom":[makeQuery(id+"F11.opExtrude","CAP_FACE",FACE,{"disambiguationData":[OSD([sQuery(id+"F0.wireOp",EDGE,"E1"),sQuery(id+"F0.wireOp",EDGE,"E5"),sQuery(id+"F0.wireOp",EDGE,"E6"),sQuery(id+"F3.wireOp",EDGE,"E13"),sQuery(id+"F3.wireOp",EDGE,"E14"),sQuery(id+"F3.wireOp",EDGE,"E15"),sQuery(id+"F3.wireOp",EDGE,"E16"),sQuery(id+"F3.wireOp",EDGE,"E17"),sQuery(id+"F3.wireOp",EDGE,"E18"),sQuery(id+"F3.wireOp",EDGE,"E19"),sQuery(id+"F3.wireOp",EDGE,"E20"),sQuery(id+"F3.wireOp",EDGE,"E21"),sQuery(id+"F3.wireOp",EDGE,"E22")])],"isStart":false}),makeQuery(id+"F15.opExtrude","SWEPT_FACE",FACE,{"disambiguationData":[OSD([sQuery(id+"F12.wireOp",EDGE,"E24")])]})]});
            var Q25;
            Q25=makeQuery(id+"F15.boolean.opBoolean","INTERSECT",EDGE,{"derivedFrom":[makeQuery(id+"F11.opExtrude","CAP_FACE",FACE,{"disambiguationData":[OSD([sQuery(id+"F0.wireOp",EDGE,"E1"),sQuery(id+"F0.wireOp",EDGE,"E5"),sQuery(id+"F0.wireOp",EDGE,"E6"),sQuery(id+"F3.wireOp",EDGE,"E13"),sQuery(id+"F3.wireOp",EDGE,"E14"),sQuery(id+"F3.wireOp",EDGE,"E15"),sQuery(id+"F3.wireOp",EDGE,"E16"),sQuery(id+"F3.wireOp",EDGE,"E17"),sQuery(id+"F3.wireOp",EDGE,"E18"),sQuery(id+"F3.wireOp",EDGE,"E19"),sQuery(id+"F3.wireOp",EDGE,"E20"),sQuery(id+"F3.wireOp",EDGE,"E21"),sQuery(id+"F3.wireOp",EDGE,"E22")])],"isStart":false}),makeQuery(id+"F15.opExtrude","SWEPT_FACE",FACE,{"disambiguationData":[OSD([sQuery(id+"F12.wireOp",EDGE,"E32")])]})]});
            var Q26;
            Q26=makeQuery(id+"F13.opExtrude","CAP_EDGE",EDGE,{"disambiguationData":[OSD([sQuery(id+"F12.wireOp",EDGE,"E35")])],"isStart":true});
            var Q27;
            Q27=makeQuery(id+"F13.opExtrude","CAP_EDGE",EDGE,{"disambiguationData":[OSD([sQuery(id+"F12.wireOp",EDGE,"E23")])],"isStart":true});
            var Q28;
            Q28=makeQuery(id+"F13.opExtrude","CAP_EDGE",EDGE,{"disambiguationData":[OSD([sQuery(id+"F12.wireOp",EDGE,"E24")])],"isStart":true});
            var Q29;
            Q29=makeQuery(id+"F13.opExtrude","CAP_EDGE",EDGE,{"disambiguationData":[OSD([sQuery(id+"F12.wireOp",EDGE,"E33")])],"isStart":true});
            var Q30;
            Q30=makeQuery(id+"F13.opExtrude","CAP_EDGE",EDGE,{"disambiguationData":[OSD([sQuery(id+"F12.wireOp",EDGE,"E32")])],"isStart":true});
            var Q31;
            Q31=makeQuery(id+"F13.opExtrude","CAP_EDGE",EDGE,{"disambiguationData":[OSD([sQuery(id+"F12.wireOp",EDGE,"E60")])],"isStart":true});
            var Q32;
            Q32=makeQuery(id+"F13.opExtrude","CAP_EDGE",EDGE,{"disambiguationData":[OSD([sQuery(id+"F12.wireOp",EDGE,"E36")])],"isStart":true});
            var Q33;
            Q33=makeQuery(id+"F13.boolean.opBoolean","SPLIT",FACE,{"disambiguationData":[TD([makeQuery(id+"F13.opExtrude","SWEPT_FACE",FACE,{"disambiguationData":[OSD([sQuery(id+"F12.wireOp",EDGE,"E36")])]})])],"derivedFrom":makeQuery(id+"F9.boolean.opBoolean","COPY",FACE,{"derivedFrom":makeQuery(id+"F9.opExtrude","CAP_FACE",FACE,{"disambiguationData":[OSD([sQuery(id+"F0.wireOp",EDGE,"E1"),sQuery(id+"F0.wireOp",EDGE,"E5"),sQuery(id+"F0.wireOp",EDGE,"E6"),sQuery(id+"F3.wireOp",EDGE,"E13"),sQuery(id+"F3.wireOp",EDGE,"E14"),sQuery(id+"F3.wireOp",EDGE,"E15"),sQuery(id+"F3.wireOp",EDGE,"E16"),sQuery(id+"F3.wireOp",EDGE,"E17"),sQuery(id+"F3.wireOp",EDGE,"E18"),sQuery(id+"F3.wireOp",EDGE,"E19"),sQuery(id+"F3.wireOp",EDGE,"E20"),sQuery(id+"F3.wireOp",EDGE,"E21"),sQuery(id+"F3.wireOp",EDGE,"E22")])],"isStart":false})})});
            var Q34;
            Q34=makeQuery(id+"F13.boolean.opBoolean","SPLIT",FACE,{"disambiguationData":[TD([makeQuery(id+"F13.opExtrude","SWEPT_FACE",FACE,{"disambiguationData":[OSD([sQuery(id+"F12.wireOp",EDGE,"E47")])]})])],"derivedFrom":makeQuery(id+"F9.boolean.opBoolean","COPY",FACE,{"derivedFrom":makeQuery(id+"F9.opExtrude","CAP_FACE",FACE,{"disambiguationData":[OSD([sQuery(id+"F0.wireOp",EDGE,"E1"),sQuery(id+"F0.wireOp",EDGE,"E5"),sQuery(id+"F0.wireOp",EDGE,"E6"),sQuery(id+"F3.wireOp",EDGE,"E13"),sQuery(id+"F3.wireOp",EDGE,"E14"),sQuery(id+"F3.wireOp",EDGE,"E15"),sQuery(id+"F3.wireOp",EDGE,"E16"),sQuery(id+"F3.wireOp",EDGE,"E17"),sQuery(id+"F3.wireOp",EDGE,"E18"),sQuery(id+"F3.wireOp",EDGE,"E19"),sQuery(id+"F3.wireOp",EDGE,"E20"),sQuery(id+"F3.wireOp",EDGE,"E21"),sQuery(id+"F3.wireOp",EDGE,"E22")])],"isStart":false})})});
            var Q35;
            Q35=makeQuery(id+"F13.boolean.opBoolean","SPLIT",FACE,{"disambiguationData":[TD([makeQuery(id+"F13.opExtrude","SWEPT_FACE",FACE,{"disambiguationData":[OSD([sQuery(id+"F12.wireOp",EDGE,"E53")])]})])],"derivedFrom":makeQuery(id+"F9.boolean.opBoolean","COPY",FACE,{"derivedFrom":makeQuery(id+"F9.opExtrude","CAP_FACE",FACE,{"disambiguationData":[OSD([sQuery(id+"F0.wireOp",EDGE,"E1"),sQuery(id+"F0.wireOp",EDGE,"E5"),sQuery(id+"F0.wireOp",EDGE,"E6"),sQuery(id+"F3.wireOp",EDGE,"E13"),sQuery(id+"F3.wireOp",EDGE,"E14"),sQuery(id+"F3.wireOp",EDGE,"E15"),sQuery(id+"F3.wireOp",EDGE,"E16"),sQuery(id+"F3.wireOp",EDGE,"E17"),sQuery(id+"F3.wireOp",EDGE,"E18"),sQuery(id+"F3.wireOp",EDGE,"E19"),sQuery(id+"F3.wireOp",EDGE,"E20"),sQuery(id+"F3.wireOp",EDGE,"E21"),sQuery(id+"F3.wireOp",EDGE,"E22")])],"isStart":false})})});
            var Q36;
            Q36=makeQuery(id+"F13.boolean.opBoolean","SPLIT",FACE,{"disambiguationData":[TD([makeQuery(id+"F13.opExtrude","SWEPT_FACE",FACE,{"disambiguationData":[OSD([sQuery(id+"F12.wireOp",EDGE,"E33")])]})])],"derivedFrom":makeQuery(id+"F9.boolean.opBoolean","COPY",FACE,{"derivedFrom":makeQuery(id+"F9.opExtrude","CAP_FACE",FACE,{"disambiguationData":[OSD([sQuery(id+"F0.wireOp",EDGE,"E1"),sQuery(id+"F0.wireOp",EDGE,"E5"),sQuery(id+"F0.wireOp",EDGE,"E6"),sQuery(id+"F3.wireOp",EDGE,"E13"),sQuery(id+"F3.wireOp",EDGE,"E14"),sQuery(id+"F3.wireOp",EDGE,"E15"),sQuery(id+"F3.wireOp",EDGE,"E16"),sQuery(id+"F3.wireOp",EDGE,"E17"),sQuery(id+"F3.wireOp",EDGE,"E18"),sQuery(id+"F3.wireOp",EDGE,"E19"),sQuery(id+"F3.wireOp",EDGE,"E20"),sQuery(id+"F3.wireOp",EDGE,"E21"),sQuery(id+"F3.wireOp",EDGE,"E22")])],"isStart":false})})});
            var Q37;
            Q37=makeQuery(id+"F13.boolean.opBoolean","SPLIT",FACE,{"disambiguationData":[TD([makeQuery(id+"F13.opExtrude","SWEPT_FACE",FACE,{"disambiguationData":[OSD([sQuery(id+"F12.wireOp",EDGE,"E50")])]})])],"derivedFrom":makeQuery(id+"F9.boolean.opBoolean","COPY",FACE,{"derivedFrom":makeQuery(id+"F9.opExtrude","CAP_FACE",FACE,{"disambiguationData":[OSD([sQuery(id+"F0.wireOp",EDGE,"E1"),sQuery(id+"F0.wireOp",EDGE,"E5"),sQuery(id+"F0.wireOp",EDGE,"E6"),sQuery(id+"F3.wireOp",EDGE,"E13"),sQuery(id+"F3.wireOp",EDGE,"E14"),sQuery(id+"F3.wireOp",EDGE,"E15"),sQuery(id+"F3.wireOp",EDGE,"E16"),sQuery(id+"F3.wireOp",EDGE,"E17"),sQuery(id+"F3.wireOp",EDGE,"E18"),sQuery(id+"F3.wireOp",EDGE,"E19"),sQuery(id+"F3.wireOp",EDGE,"E20"),sQuery(id+"F3.wireOp",EDGE,"E21"),sQuery(id+"F3.wireOp",EDGE,"E22")])],"isStart":false})})});
            var Q38;
            Q38=makeQuery(id+"F13.boolean.opBoolean","SPLIT",FACE,{"disambiguationData":[TD([makeQuery(id+"F13.opExtrude","SWEPT_FACE",FACE,{"disambiguationData":[OSD([sQuery(id+"F12.wireOp",EDGE,"E41")])]})])],"derivedFrom":makeQuery(id+"F9.boolean.opBoolean","COPY",FACE,{"derivedFrom":makeQuery(id+"F9.opExtrude","CAP_FACE",FACE,{"disambiguationData":[OSD([sQuery(id+"F0.wireOp",EDGE,"E1"),sQuery(id+"F0.wireOp",EDGE,"E5"),sQuery(id+"F0.wireOp",EDGE,"E6"),sQuery(id+"F3.wireOp",EDGE,"E13"),sQuery(id+"F3.wireOp",EDGE,"E14"),sQuery(id+"F3.wireOp",EDGE,"E15"),sQuery(id+"F3.wireOp",EDGE,"E16"),sQuery(id+"F3.wireOp",EDGE,"E17"),sQuery(id+"F3.wireOp",EDGE,"E18"),sQuery(id+"F3.wireOp",EDGE,"E19"),sQuery(id+"F3.wireOp",EDGE,"E20"),sQuery(id+"F3.wireOp",EDGE,"E21"),sQuery(id+"F3.wireOp",EDGE,"E22")])],"isStart":false})})});
            var Q39;
            Q39=makeQuery(id+"F13.opExtrude","CAP_EDGE",EDGE,{"disambiguationData":[OSD([sQuery(id+"F12.wireOp",EDGE,"E58")])],"isStart":true});
            var Q40;
            Q40=makeQuery(id+"F13.opExtrude","CAP_EDGE",EDGE,{"disambiguationData":[OSD([sQuery(id+"F12.wireOp",EDGE,"E31")])],"isStart":true});
            var Q41;
            Q41=makeQuery(id+"F13.opExtrude","CAP_EDGE",EDGE,{"disambiguationData":[OSD([sQuery(id+"F12.wireOp",EDGE,"E30")])],"isStart":true});
            var Q42;
            Q42=makeQuery(id+"F13.opExtrude","CAP_EDGE",EDGE,{"disambiguationData":[OSD([sQuery(id+"F12.wireOp",EDGE,"E57")])],"isStart":true});
            var Q43;
            Q43=makeQuery(id+"F13.opExtrude","CAP_EDGE",EDGE,{"disambiguationData":[OSD([sQuery(id+"F12.wireOp",EDGE,"E29")])],"isStart":true});
            var Q44;
            Q44=makeQuery(id+"F13.opExtrude","CAP_EDGE",EDGE,{"disambiguationData":[OSD([sQuery(id+"F12.wireOp",EDGE,"E80")])],"isStart":true});
            var Q45;
            Q45=makeQuery(id+"F13.opExtrude","CAP_EDGE",EDGE,{"disambiguationData":[OSD([sQuery(id+"F12.wireOp",EDGE,"E39")])],"isStart":true});
            var Q46;
            Q46=makeQuery(id+"F13.opExtrude","CAP_EDGE",EDGE,{"disambiguationData":[OSD([sQuery(id+"F12.wireOp",EDGE,"E78")])],"isStart":true});
            var Q47;
            Q47=makeQuery(id+"F13.opExtrude","CAP_EDGE",EDGE,{"disambiguationData":[OSD([sQuery(id+"F12.wireOp",EDGE,"E75")])],"isStart":true});
            var Q48;
            Q48=makeQuery(id+"F13.opExtrude","CAP_EDGE",EDGE,{"disambiguationData":[OSD([sQuery(id+"F12.wireOp",EDGE,"E40")])],"isStart":true});
            var Q49;
            Q49=makeQuery(id+"F13.opExtrude","CAP_EDGE",EDGE,{"disambiguationData":[OSD([sQuery(id+"F12.wireOp",EDGE,"E74")])],"isStart":true});
            var Q50;
            Q50=makeQuery(id+"F13.opExtrude","CAP_EDGE",EDGE,{"disambiguationData":[OSD([sQuery(id+"F12.wireOp",EDGE,"E28")])],"isStart":true});
            var Q51;
            Q51=makeQuery(id+"F13.opExtrude","CAP_EDGE",EDGE,{"disambiguationData":[OSD([sQuery(id+"F12.wireOp",EDGE,"E72")])],"isStart":true});
            var Q52;
            Q52=makeQuery(id+"F13.opExtrude","CAP_EDGE",EDGE,{"disambiguationData":[OSD([sQuery(id+"F12.wireOp",EDGE,"E27")])],"isStart":true});
            var Q53;
            Q53=makeQuery(id+"F13.opExtrude","CAP_EDGE",EDGE,{"disambiguationData":[OSD([sQuery(id+"F12.wireOp",EDGE,"E26")])],"isStart":true});
            var Q54;
            Q54=makeQuery(id+"F13.opExtrude","CAP_EDGE",EDGE,{"disambiguationData":[OSD([sQuery(id+"F12.wireOp",EDGE,"E68")])],"isStart":true});
            var Q55;
            Q55=makeQuery(id+"F13.opExtrude","CAP_EDGE",EDGE,{"disambiguationData":[OSD([sQuery(id+"F12.wireOp",EDGE,"E25")])],"isStart":true});
            fillet(context, id + "F20", {"entities" : qUnion([Q0, Q1, Q2, Q3, Q4, Q5, Q6, Q7, Q8, Q9, Q10, Q11, Q12, Q13, Q14, Q15, Q16, Q17, Q18, Q19, Q20, Q21, Q22, Q23, Q24, Q25, Q26, Q27, Q28, Q29, Q30, Q31, Q32, Q33, Q34, Q35, Q36, Q37, Q38, Q39, Q40, Q41, Q42, Q43, Q44, Q45, Q46, Q47, Q48, Q49, Q50, Q51, Q52, Q53, Q54, Q55]), "radius" : 0.25 * mm, "tangentPropagation" : true, "allowEdgeOverflow" : false});
        }
    });
